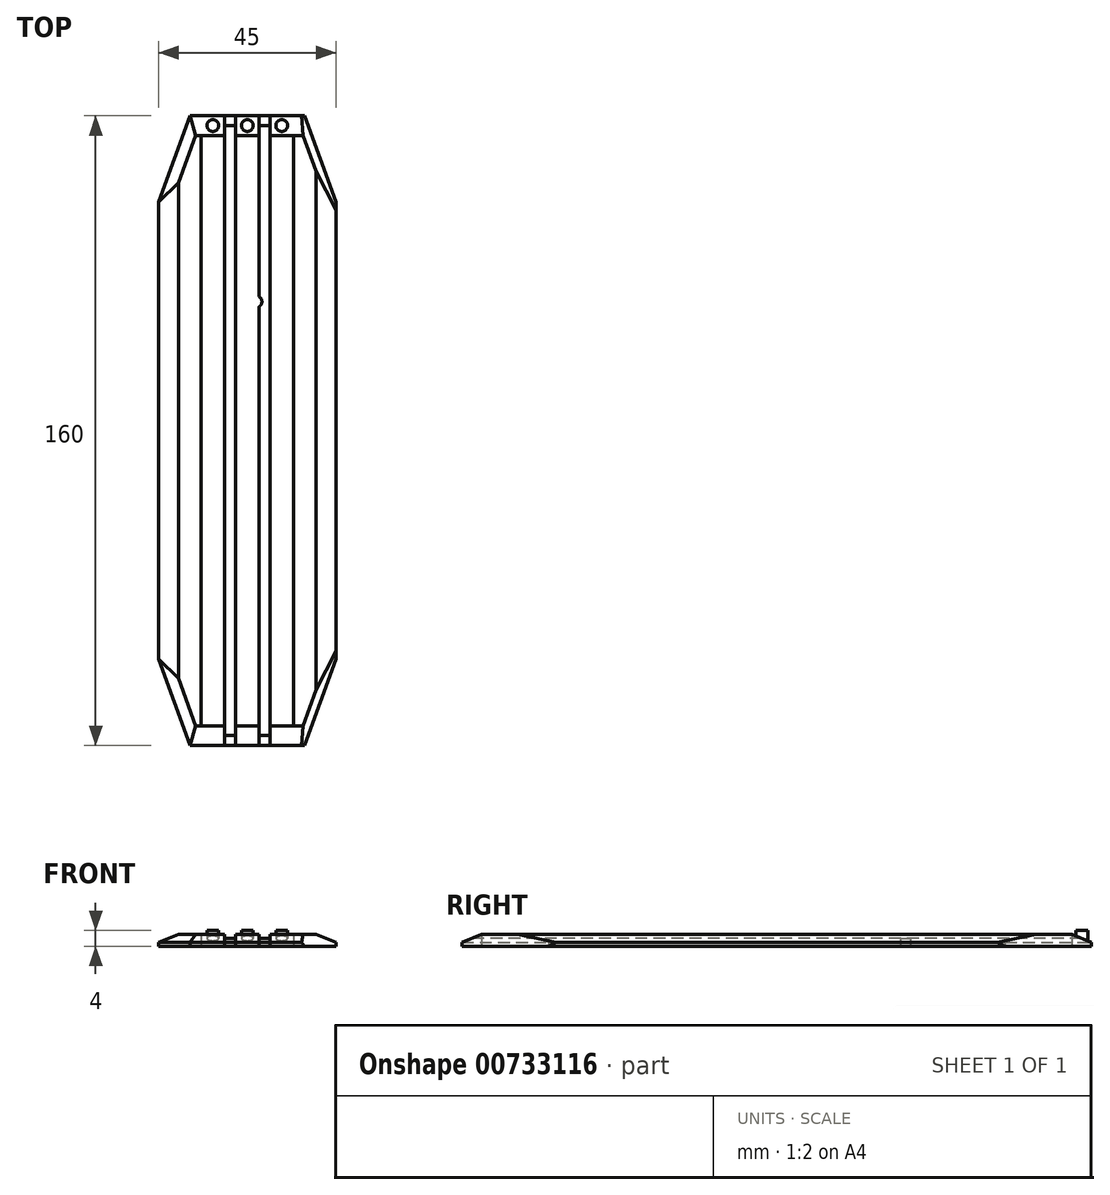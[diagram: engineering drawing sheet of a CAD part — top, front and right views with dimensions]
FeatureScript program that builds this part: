
annotation { "Feature Type Name" : "Feature", "Feature Type Description" : "" }
export const myFeature = defineFeature(function(context is Context, id is Id, definition is map)
    precondition{}
    {
        {
            var Q0;
            Q0=qCreatedBy(makeId("Top.planeOp"),FACE);
            var sketch = newSketch(context, id + "F0", { "sketchPlane" : qUnion([Q0])});
            skLineSegment(sketch, "E0.bottom", {"start": v(-22.12, 90) * mm, "end": v(22.88, 90) * mm});
            skLineSegment(sketch, "E0.top", {"start": v(-22.12, -70) * mm, "end": v(22.88, -70) * mm});
            skLineSegment(sketch, "E0.left", {"start": v(-22.12, 90) * mm, "end": v(-22.12, -70) * mm});
            skLineSegment(sketch, "E0.right", {"start": v(22.88, 90) * mm, "end": v(22.88, -70) * mm});
            skLineSegment(sketch, "E1", {"start": v(-22.12, 68) * mm, "end": v(-14.12, 90) * mm});
            skLineSegment(sketch, "E2", {"start": v(14.88, 90) * mm, "end": v(22.88, 68) * mm});
            skLineSegment(sketch, "E3", {"start": v(-22.12, -48) * mm, "end": v(-14.12, -70) * mm});
            skLineSegment(sketch, "E4", {"start": v(14.88, -70) * mm, "end": v(22.88, -48) * mm});
            skLineSegment(sketch, "E5", {"start": v(-11.37, 90) * mm, "end": v(-11.37, -70) * mm});
            skLineSegment(sketch, "E6", {"start": v(-5.37, 90) * mm, "end": v(-5.37, -70) * mm});
            skLineSegment(sketch, "E7", {"start": v(-2.62, 90) * mm, "end": v(-2.62, -70) * mm});
            skLineSegment(sketch, "E8", {"start": v(3.38, 90) * mm, "end": v(3.38, -70) * mm});
            skLineSegment(sketch, "E9", {"start": v(6.13, 90) * mm, "end": v(6.13, -70) * mm});
            skLineSegment(sketch, "E10", {"start": v(12.13, 90) * mm, "end": v(12.13, -70) * mm});
            skLineSegment(sketch, "E11", {"start": v(-22.12, 85) * mm, "end": v(22.88, 85) * mm});
            skLineSegment(sketch, "E12", {"start": v(-22.12, 80) * mm, "end": v(22.88, 80) * mm});
            skLineSegment(sketch, "E13", {"start": v(-22.12, 75) * mm, "end": v(22.88, 75) * mm});
            skLineSegment(sketch, "E14", {"start": v(-22.12, 70) * mm, "end": v(22.15, 70) * mm});
            skLineSegment(sketch, "E15", {"start": v(-22.12, 65) * mm, "end": v(22.88, 65) * mm});
            skLineSegment(sketch, "E16", {"start": v(-22.12, 60) * mm, "end": v(22.88, 60) * mm});
            skLineSegment(sketch, "E17", {"start": v(-22.12, 55) * mm, "end": v(22.88, 55) * mm});
            skLineSegment(sketch, "E18", {"start": v(-22.12, 50) * mm, "end": v(22.88, 50) * mm});
            skLineSegment(sketch, "E19", {"start": v(-22.12, 45) * mm, "end": v(22.88, 45) * mm});
            skLineSegment(sketch, "E20", {"start": v(-22.12, 40) * mm, "end": v(22.88, 40) * mm});
            skLineSegment(sketch, "E21", {"start": v(-22.12, 35) * mm, "end": v(22.88, 35) * mm});
            skLineSegment(sketch, "E22", {"start": v(-22.12, 30) * mm, "end": v(22.88, 30) * mm});
            skLineSegment(sketch, "E23", {"start": v(-22.12, 25) * mm, "end": v(22.88, 25) * mm});
            skLineSegment(sketch, "E24", {"start": v(-22.12, 20) * mm, "end": v(22.88, 20) * mm});
            skLineSegment(sketch, "E25", {"start": v(-22.12, 10) * mm, "end": v(22.88, 10) * mm});
            skLineSegment(sketch, "E26", {"start": v(-22.12, 5) * mm, "end": v(22.88, 5) * mm});
            skLineSegment(sketch, "E27", {"start": v(-22.12, 0) * mm, "end": v(22.88, 0) * mm});
            skLineSegment(sketch, "E28", {"start": v(-22.12, 15) * mm, "end": v(22.88, 15) * mm});
            skLineSegment(sketch, "E29", {"start": v(-22.12, -5) * mm, "end": v(22.88, -5) * mm});
            skLineSegment(sketch, "E30", {"start": v(-22.12, -10) * mm, "end": v(22.88, -10) * mm});
            skLineSegment(sketch, "E31", {"start": v(-22.12, -15) * mm, "end": v(22.88, -15) * mm});
            skLineSegment(sketch, "E32", {"start": v(-22.12, -20) * mm, "end": v(22.88, -20) * mm});
            skLineSegment(sketch, "E33", {"start": v(-22.12, -25) * mm, "end": v(22.88, -25) * mm});
            skLineSegment(sketch, "E34", {"start": v(-22.12, -30) * mm, "end": v(22.88, -30) * mm});
            skLineSegment(sketch, "E35", {"start": v(-22.12, -35) * mm, "end": v(22.88, -35) * mm});
            skLineSegment(sketch, "E36", {"start": v(-22.12, -40) * mm, "end": v(22.88, -40) * mm});
            skLineSegment(sketch, "E37", {"start": v(-22.12, -45) * mm, "end": v(22.88, -45) * mm});
            skLineSegment(sketch, "E38", {"start": v(-22.12, -50) * mm, "end": v(22.88, -50) * mm});
            skLineSegment(sketch, "E39", {"start": v(-22.12, -55) * mm, "end": v(22.88, -55) * mm});
            skLineSegment(sketch, "E40", {"start": v(-22.12, -60) * mm, "end": v(22.88, -60) * mm});
            skLineSegment(sketch, "E41", {"start": v(-22.12, -65) * mm, "end": v(22.88, -65) * mm});
            skCircle(sketch, "E42", {"center": v(-8.37, -62.5) * mm, "radius": 1.5 * mm});
            skLineSegment(sketch, "E43", {"start": v(-9.02, -61.15) * mm, "end": v(-7.02, -63.15) * mm});
            skLineSegment(sketch, "E44", {"start": v(-9.73, -61.85) * mm, "end": v(-7.73, -63.85) * mm});
            skLineSegment(sketch, "E45", {"start": v(-7.73, -61.15) * mm, "end": v(-9.73, -63.15) * mm});
            skLineSegment(sketch, "E46", {"start": v(-7.02, -61.85) * mm, "end": v(-9.02, -63.85) * mm});
            skCircle(sketch, "E47", {"center": v(9.13, -62.5) * mm, "radius": 1.5 * mm});
            skLineSegment(sketch, "E48", {"start": v(8.48, -61.15) * mm, "end": v(10.48, -63.15) * mm});
            skLineSegment(sketch, "E49", {"start": v(7.77, -61.85) * mm, "end": v(9.77, -63.85) * mm});
            skLineSegment(sketch, "E50", {"start": v(9.77, -61.15) * mm, "end": v(7.77, -63.15) * mm});
            skLineSegment(sketch, "E51", {"start": v(10.48, -61.85) * mm, "end": v(8.48, -63.85) * mm});
            skCircle(sketch, "E52", {"center": v(0.38, -62.5) * mm, "radius": 1.5 * mm});
            skLineSegment(sketch, "E53", {"start": v(-0.27, -61.15) * mm, "end": v(1.73, -63.15) * mm});
            skLineSegment(sketch, "E54", {"start": v(-0.98, -61.85) * mm, "end": v(1.02, -63.85) * mm});
            skLineSegment(sketch, "E55", {"start": v(1.02, -61.15) * mm, "end": v(-0.98, -63.15) * mm});
            skLineSegment(sketch, "E56", {"start": v(1.73, -61.85) * mm, "end": v(-0.27, -63.85) * mm});
            skCircle(sketch, "E57", {"center": v(9.19, -57.36) * mm, "radius": 1.5 * mm});
            skLineSegment(sketch, "E58", {"start": v(8.54, -56) * mm, "end": v(10.54, -58) * mm});
            skLineSegment(sketch, "E59", {"start": v(7.83, -56.7) * mm, "end": v(9.83, -58.7) * mm});
            skLineSegment(sketch, "E60", {"start": v(9.83, -56) * mm, "end": v(7.83, -58) * mm});
            skLineSegment(sketch, "E61", {"start": v(10.54, -56.7) * mm, "end": v(8.54, -58.7) * mm});
            skCircle(sketch, "E62", {"center": v(0.75, -56.96) * mm, "radius": 1.5 * mm});
            skLineSegment(sketch, "E63", {"start": v(0.1, -55.6) * mm, "end": v(2.1, -57.6) * mm});
            skLineSegment(sketch, "E64", {"start": v(-0.6, -56.31) * mm, "end": v(1.4, -58.31) * mm});
            skLineSegment(sketch, "E65", {"start": v(1.4, -55.6) * mm, "end": v(-0.6, -57.6) * mm});
            skLineSegment(sketch, "E66", {"start": v(2.1, -56.31) * mm, "end": v(0.1, -58.31) * mm});
            skCircle(sketch, "E67", {"center": v(-8.3, -57.32) * mm, "radius": 1.5 * mm});
            skLineSegment(sketch, "E68", {"start": v(-8.95, -55.97) * mm, "end": v(-6.95, -57.97) * mm});
            skLineSegment(sketch, "E69", {"start": v(-9.66, -56.68) * mm, "end": v(-7.66, -58.68) * mm});
            skLineSegment(sketch, "E70", {"start": v(-7.66, -55.97) * mm, "end": v(-9.66, -57.97) * mm});
            skLineSegment(sketch, "E71", {"start": v(-6.95, -56.68) * mm, "end": v(-8.95, -58.68) * mm});
            skCircle(sketch, "E72", {"center": v(-8.54, -52.38) * mm, "radius": 1.5 * mm});
            skLineSegment(sketch, "E73", {"start": v(-9.19, -51.03) * mm, "end": v(-7.19, -53.03) * mm});
            skLineSegment(sketch, "E74", {"start": v(-9.9, -51.74) * mm, "end": v(-7.9, -53.74) * mm});
            skLineSegment(sketch, "E75", {"start": v(-7.9, -51.03) * mm, "end": v(-9.9, -53.03) * mm});
            skLineSegment(sketch, "E76", {"start": v(-7.19, -51.74) * mm, "end": v(-9.19, -53.74) * mm});
            skCircle(sketch, "E77", {"center": v(0.5, -52.63) * mm, "radius": 1.5 * mm});
            skLineSegment(sketch, "E78", {"start": v(-0.15, -51.28) * mm, "end": v(1.85, -53.28) * mm});
            skLineSegment(sketch, "E79", {"start": v(-0.85, -51.99) * mm, "end": v(1.15, -53.99) * mm});
            skLineSegment(sketch, "E80", {"start": v(1.15, -51.28) * mm, "end": v(-0.85, -53.28) * mm});
            skLineSegment(sketch, "E81", {"start": v(1.85, -51.99) * mm, "end": v(-0.15, -53.99) * mm});
            skCircle(sketch, "E82", {"center": v(9.29, -52.38) * mm, "radius": 1.5 * mm});
            skLineSegment(sketch, "E83", {"start": v(8.64, -51.03) * mm, "end": v(10.64, -53.03) * mm});
            skLineSegment(sketch, "E84", {"start": v(7.94, -51.74) * mm, "end": v(9.94, -53.74) * mm});
            skLineSegment(sketch, "E85", {"start": v(9.94, -51.03) * mm, "end": v(7.94, -53.03) * mm});
            skLineSegment(sketch, "E86", {"start": v(10.64, -51.74) * mm, "end": v(8.64, -53.74) * mm});
            skCircle(sketch, "E87", {"center": v(9.04, -47.23) * mm, "radius": 1.5 * mm});
            skLineSegment(sketch, "E88", {"start": v(8.4, -45.88) * mm, "end": v(10.4, -47.88) * mm});
            skLineSegment(sketch, "E89", {"start": v(7.68, -46.59) * mm, "end": v(9.68, -48.59) * mm});
            skLineSegment(sketch, "E90", {"start": v(9.68, -45.88) * mm, "end": v(7.68, -47.88) * mm});
            skLineSegment(sketch, "E91", {"start": v(10.4, -46.59) * mm, "end": v(8.4, -48.59) * mm});
            skCircle(sketch, "E92", {"center": v(0.04, -47.48) * mm, "radius": 1.5 * mm});
            skLineSegment(sketch, "E93", {"start": v(-0.6, -46.13) * mm, "end": v(1.4, -48.13) * mm});
            skLineSegment(sketch, "E94", {"start": v(-1.32, -46.84) * mm, "end": v(0.68, -48.84) * mm});
            skLineSegment(sketch, "E95", {"start": v(0.68, -46.13) * mm, "end": v(-1.32, -48.13) * mm});
            skLineSegment(sketch, "E96", {"start": v(1.4, -46.84) * mm, "end": v(-0.6, -48.84) * mm});
            skCircle(sketch, "E97", {"center": v(-7.79, -47.1) * mm, "radius": 1.5 * mm});
            skLineSegment(sketch, "E98", {"start": v(-8.43, -45.75) * mm, "end": v(-6.43, -47.75) * mm});
            skLineSegment(sketch, "E99", {"start": v(-9.14, -46.46) * mm, "end": v(-7.14, -48.46) * mm});
            skLineSegment(sketch, "E100", {"start": v(-7.14, -45.75) * mm, "end": v(-9.14, -47.75) * mm});
            skLineSegment(sketch, "E101", {"start": v(-6.43, -46.46) * mm, "end": v(-8.43, -48.46) * mm});
            skCircle(sketch, "E102", {"center": v(-8.3, -42.65) * mm, "radius": 1.5 * mm});
            skLineSegment(sketch, "E103", {"start": v(-8.94, -41.3) * mm, "end": v(-6.94, -43.3) * mm});
            skLineSegment(sketch, "E104", {"start": v(-9.64, -42) * mm, "end": v(-7.64, -44) * mm});
            skLineSegment(sketch, "E105", {"start": v(-7.64, -41.3) * mm, "end": v(-9.64, -43.3) * mm});
            skLineSegment(sketch, "E106", {"start": v(-6.94, -42) * mm, "end": v(-8.94, -44) * mm});
            skCircle(sketch, "E107", {"center": v(-8.67, -37.44) * mm, "radius": 1.5 * mm});
            skLineSegment(sketch, "E108", {"start": v(-9.31, -36.09) * mm, "end": v(-7.31, -38.09) * mm});
            skLineSegment(sketch, "E109", {"start": v(-10.02, -36.8) * mm, "end": v(-8.02, -38.8) * mm});
            skLineSegment(sketch, "E110", {"start": v(-8.02, -36.09) * mm, "end": v(-10.02, -38.09) * mm});
            skLineSegment(sketch, "E111", {"start": v(-7.31, -36.8) * mm, "end": v(-9.31, -38.8) * mm});
            skCircle(sketch, "E112", {"center": v(-8.3, -32.42) * mm, "radius": 1.5 * mm});
            skLineSegment(sketch, "E113", {"start": v(-8.94, -31.06) * mm, "end": v(-6.94, -33.06) * mm});
            skLineSegment(sketch, "E114", {"start": v(-9.64, -31.77) * mm, "end": v(-7.64, -33.77) * mm});
            skLineSegment(sketch, "E115", {"start": v(-7.64, -31.06) * mm, "end": v(-9.64, -33.06) * mm});
            skLineSegment(sketch, "E116", {"start": v(-6.94, -31.77) * mm, "end": v(-8.94, -33.77) * mm});
            skCircle(sketch, "E117", {"center": v(-8.42, -27.14) * mm, "radius": 1.5 * mm});
            skLineSegment(sketch, "E118", {"start": v(-9.06, -25.79) * mm, "end": v(-7.06, -27.79) * mm});
            skLineSegment(sketch, "E119", {"start": v(-9.77, -26.5) * mm, "end": v(-7.77, -28.5) * mm});
            skLineSegment(sketch, "E120", {"start": v(-7.77, -25.79) * mm, "end": v(-9.77, -27.79) * mm});
            skLineSegment(sketch, "E121", {"start": v(-7.06, -26.5) * mm, "end": v(-9.06, -28.5) * mm});
            skCircle(sketch, "E122", {"center": v(0.06, -27.52) * mm, "radius": 1.5 * mm});
            skLineSegment(sketch, "E123", {"start": v(-0.59, -26.16) * mm, "end": v(1.41, -28.16) * mm});
            skLineSegment(sketch, "E124", {"start": v(-1.3, -26.87) * mm, "end": v(0.7, -28.87) * mm});
            skLineSegment(sketch, "E125", {"start": v(0.7, -26.16) * mm, "end": v(-1.3, -28.16) * mm});
            skLineSegment(sketch, "E126", {"start": v(1.41, -26.87) * mm, "end": v(-0.59, -28.87) * mm});
            skCircle(sketch, "E127", {"center": v(0.06, -32.35) * mm, "radius": 1.5 * mm});
            skLineSegment(sketch, "E128", {"start": v(-0.59, -31) * mm, "end": v(1.41, -33) * mm});
            skLineSegment(sketch, "E129", {"start": v(-1.3, -31.7) * mm, "end": v(0.7, -33.7) * mm});
            skLineSegment(sketch, "E130", {"start": v(0.7, -31) * mm, "end": v(-1.3, -33) * mm});
            skLineSegment(sketch, "E131", {"start": v(1.41, -31.7) * mm, "end": v(-0.59, -33.7) * mm});
            skCircle(sketch, "E132", {"center": v(0.25, -37.44) * mm, "radius": 1.5 * mm});
            skLineSegment(sketch, "E133", {"start": v(-0.4, -36.09) * mm, "end": v(1.6, -38.09) * mm});
            skLineSegment(sketch, "E134", {"start": v(-1.1, -36.8) * mm, "end": v(0.9, -38.8) * mm});
            skLineSegment(sketch, "E135", {"start": v(0.9, -36.09) * mm, "end": v(-1.1, -38.09) * mm});
            skLineSegment(sketch, "E136", {"start": v(1.6, -36.8) * mm, "end": v(-0.4, -38.8) * mm});
            skCircle(sketch, "E137", {"center": v(0.37, -42.4) * mm, "radius": 1.5 * mm});
            skLineSegment(sketch, "E138", {"start": v(-0.27, -41.05) * mm, "end": v(1.73, -43.05) * mm});
            skLineSegment(sketch, "E139", {"start": v(-0.98, -41.75) * mm, "end": v(1.02, -43.75) * mm});
            skLineSegment(sketch, "E140", {"start": v(1.02, -41.05) * mm, "end": v(-0.98, -43.05) * mm});
            skLineSegment(sketch, "E141", {"start": v(1.73, -41.75) * mm, "end": v(-0.27, -43.75) * mm});
            skCircle(sketch, "E142", {"center": v(9.8, -42.08) * mm, "radius": 1.5 * mm});
            skLineSegment(sketch, "E143", {"start": v(9.15, -40.73) * mm, "end": v(11.15, -42.73) * mm});
            skLineSegment(sketch, "E144", {"start": v(8.44, -41.44) * mm, "end": v(10.44, -43.44) * mm});
            skLineSegment(sketch, "E145", {"start": v(10.44, -40.73) * mm, "end": v(8.44, -42.73) * mm});
            skLineSegment(sketch, "E146", {"start": v(11.15, -41.44) * mm, "end": v(9.15, -43.44) * mm});
            skCircle(sketch, "E147", {"center": v(9.29, -37.06) * mm, "radius": 1.5 * mm});
            skLineSegment(sketch, "E148", {"start": v(8.64, -35.7) * mm, "end": v(10.64, -37.7) * mm});
            skLineSegment(sketch, "E149", {"start": v(7.94, -36.42) * mm, "end": v(9.94, -38.42) * mm});
            skLineSegment(sketch, "E150", {"start": v(9.94, -35.7) * mm, "end": v(7.94, -37.7) * mm});
            skLineSegment(sketch, "E151", {"start": v(10.64, -36.42) * mm, "end": v(8.64, -38.42) * mm});
            skCircle(sketch, "E152", {"center": v(9.35, -32.1) * mm, "radius": 1.5 * mm});
            skLineSegment(sketch, "E153", {"start": v(8.7, -30.75) * mm, "end": v(10.7, -32.75) * mm});
            skLineSegment(sketch, "E154", {"start": v(8, -31.46) * mm, "end": v(10, -33.46) * mm});
            skLineSegment(sketch, "E155", {"start": v(10, -30.75) * mm, "end": v(8, -32.75) * mm});
            skLineSegment(sketch, "E156", {"start": v(10.7, -31.46) * mm, "end": v(8.7, -33.46) * mm});
            skCircle(sketch, "E157", {"center": v(9.04, -27.77) * mm, "radius": 1.5 * mm});
            skLineSegment(sketch, "E158", {"start": v(8.4, -26.42) * mm, "end": v(10.4, -28.42) * mm});
            skLineSegment(sketch, "E159", {"start": v(7.68, -27.12) * mm, "end": v(9.68, -29.12) * mm});
            skLineSegment(sketch, "E160", {"start": v(9.68, -26.42) * mm, "end": v(7.68, -28.42) * mm});
            skLineSegment(sketch, "E161", {"start": v(10.4, -27.12) * mm, "end": v(8.4, -29.12) * mm});
            skCircle(sketch, "E162", {"center": v(9.1, -22.4) * mm, "radius": 1.5 * mm});
            skLineSegment(sketch, "E163", {"start": v(8.45, -21.05) * mm, "end": v(10.45, -23.05) * mm});
            skLineSegment(sketch, "E164", {"start": v(7.74, -21.75) * mm, "end": v(9.74, -23.75) * mm});
            skLineSegment(sketch, "E165", {"start": v(9.74, -21.05) * mm, "end": v(7.74, -23.05) * mm});
            skLineSegment(sketch, "E166", {"start": v(10.45, -21.75) * mm, "end": v(8.45, -23.75) * mm});
            skCircle(sketch, "E167", {"center": v(9.15, -17.23) * mm, "radius": 1.5 * mm});
            skLineSegment(sketch, "E168", {"start": v(8.5, -15.87) * mm, "end": v(10.5, -17.87) * mm});
            skLineSegment(sketch, "E169", {"start": v(7.8, -16.58) * mm, "end": v(9.8, -18.58) * mm});
            skLineSegment(sketch, "E170", {"start": v(9.8, -15.87) * mm, "end": v(7.8, -17.87) * mm});
            skLineSegment(sketch, "E171", {"start": v(10.5, -16.58) * mm, "end": v(8.5, -18.58) * mm});
            skCircle(sketch, "E172", {"center": v(8.91, -12.1) * mm, "radius": 1.5 * mm});
            skLineSegment(sketch, "E173", {"start": v(8.26, -10.75) * mm, "end": v(10.26, -12.75) * mm});
            skLineSegment(sketch, "E174", {"start": v(7.56, -11.46) * mm, "end": v(9.56, -13.46) * mm});
            skLineSegment(sketch, "E175", {"start": v(9.56, -10.75) * mm, "end": v(7.56, -12.75) * mm});
            skLineSegment(sketch, "E176", {"start": v(10.26, -11.46) * mm, "end": v(8.26, -13.46) * mm});
            skCircle(sketch, "E177", {"center": v(8.91, -6.98) * mm, "radius": 1.5 * mm});
            skLineSegment(sketch, "E178", {"start": v(8.26, -5.63) * mm, "end": v(10.26, -7.63) * mm});
            skLineSegment(sketch, "E179", {"start": v(7.56, -6.33) * mm, "end": v(9.56, -8.33) * mm});
            skLineSegment(sketch, "E180", {"start": v(9.56, -5.63) * mm, "end": v(7.56, -7.63) * mm});
            skLineSegment(sketch, "E181", {"start": v(10.26, -6.33) * mm, "end": v(8.26, -8.33) * mm});
            skCircle(sketch, "E182", {"center": v(8.67, -2.47) * mm, "radius": 1.5 * mm});
            skLineSegment(sketch, "E183", {"start": v(8.02, -1.11) * mm, "end": v(10.02, -3.11) * mm});
            skLineSegment(sketch, "E184", {"start": v(7.31, -1.82) * mm, "end": v(9.31, -3.82) * mm});
            skLineSegment(sketch, "E185", {"start": v(9.31, -1.11) * mm, "end": v(7.31, -3.11) * mm});
            skLineSegment(sketch, "E186", {"start": v(10.02, -1.82) * mm, "end": v(8.02, -3.82) * mm});
            skCircle(sketch, "E187", {"center": v(8.54, 2.05) * mm, "radius": 1.5 * mm});
            skLineSegment(sketch, "E188", {"start": v(7.9, 3.4) * mm, "end": v(9.9, 1.4) * mm});
            skLineSegment(sketch, "E189", {"start": v(7.2, 2.7) * mm, "end": v(9.2, 0.7) * mm});
            skLineSegment(sketch, "E190", {"start": v(9.2, 3.4) * mm, "end": v(7.2, 1.4) * mm});
            skLineSegment(sketch, "E191", {"start": v(9.9, 2.7) * mm, "end": v(7.9, 0.7) * mm});
            skCircle(sketch, "E192", {"center": v(-0.3, 2.54) * mm, "radius": 1.5 * mm});
            skLineSegment(sketch, "E193", {"start": v(-0.95, 3.9) * mm, "end": v(1.05, 1.9) * mm});
            skLineSegment(sketch, "E194", {"start": v(-1.65, 3.18) * mm, "end": v(0.35, 1.18) * mm});
            skLineSegment(sketch, "E195", {"start": v(0.35, 3.9) * mm, "end": v(-1.65, 1.9) * mm});
            skLineSegment(sketch, "E196", {"start": v(1.05, 3.18) * mm, "end": v(-0.95, 1.18) * mm});
            skCircle(sketch, "E197", {"center": v(0.19, -3.5) * mm, "radius": 1.5 * mm});
            skLineSegment(sketch, "E198", {"start": v(-0.46, -2.15) * mm, "end": v(1.54, -4.15) * mm});
            skLineSegment(sketch, "E199", {"start": v(-1.17, -2.86) * mm, "end": v(0.83, -4.86) * mm});
            skLineSegment(sketch, "E200", {"start": v(0.83, -2.15) * mm, "end": v(-1.17, -4.15) * mm});
            skLineSegment(sketch, "E201", {"start": v(1.54, -2.86) * mm, "end": v(-0.46, -4.86) * mm});
            skCircle(sketch, "E202", {"center": v(0.13, -7.22) * mm, "radius": 1.5 * mm});
            skLineSegment(sketch, "E203", {"start": v(-0.52, -5.87) * mm, "end": v(1.48, -7.87) * mm});
            skLineSegment(sketch, "E204", {"start": v(-1.23, -6.58) * mm, "end": v(0.77, -8.58) * mm});
            skLineSegment(sketch, "E205", {"start": v(0.77, -5.87) * mm, "end": v(-1.23, -7.87) * mm});
            skLineSegment(sketch, "E206", {"start": v(1.48, -6.58) * mm, "end": v(-0.52, -8.58) * mm});
            skCircle(sketch, "E207", {"center": v(0.86, -13.44) * mm, "radius": 1.5 * mm});
            skLineSegment(sketch, "E208", {"start": v(0.21, -12.1) * mm, "end": v(2.21, -14.1) * mm});
            skLineSegment(sketch, "E209", {"start": v(-0.5, -12.8) * mm, "end": v(1.5, -14.8) * mm});
            skLineSegment(sketch, "E210", {"start": v(1.5, -12.1) * mm, "end": v(-0.5, -14.1) * mm});
            skLineSegment(sketch, "E211", {"start": v(2.21, -12.8) * mm, "end": v(0.21, -14.8) * mm});
            skCircle(sketch, "E212", {"center": v(0.5, -17.35) * mm, "radius": 1.5 * mm});
            skLineSegment(sketch, "E213", {"start": v(-0.15, -16) * mm, "end": v(1.85, -18) * mm});
            skLineSegment(sketch, "E214", {"start": v(-0.86, -16.7) * mm, "end": v(1.14, -18.7) * mm});
            skLineSegment(sketch, "E215", {"start": v(1.14, -16) * mm, "end": v(-0.86, -18) * mm});
            skLineSegment(sketch, "E216", {"start": v(1.85, -16.7) * mm, "end": v(-0.15, -18.7) * mm});
            skCircle(sketch, "E217", {"center": v(0.37, -22.05) * mm, "radius": 1.5 * mm});
            skLineSegment(sketch, "E218", {"start": v(-0.28, -20.7) * mm, "end": v(1.72, -22.7) * mm});
            skLineSegment(sketch, "E219", {"start": v(-0.98, -21.4) * mm, "end": v(1.02, -23.4) * mm});
            skLineSegment(sketch, "E220", {"start": v(1.02, -20.7) * mm, "end": v(-0.98, -22.7) * mm});
            skLineSegment(sketch, "E221", {"start": v(1.72, -21.4) * mm, "end": v(-0.28, -23.4) * mm});
            skCircle(sketch, "E222", {"center": v(-8.78, -22.47) * mm, "radius": 1.5 * mm});
            skLineSegment(sketch, "E223", {"start": v(-9.43, -21.12) * mm, "end": v(-7.43, -23.12) * mm});
            skLineSegment(sketch, "E224", {"start": v(-10.13, -21.83) * mm, "end": v(-8.13, -23.83) * mm});
            skLineSegment(sketch, "E225", {"start": v(-8.13, -21.12) * mm, "end": v(-10.13, -23.12) * mm});
            skLineSegment(sketch, "E226", {"start": v(-7.43, -21.83) * mm, "end": v(-9.43, -23.83) * mm});
            skCircle(sketch, "E227", {"center": v(-8.35, -17.9) * mm, "radius": 1.5 * mm});
            skLineSegment(sketch, "E228", {"start": v(-9, -16.54) * mm, "end": v(-7, -18.54) * mm});
            skLineSegment(sketch, "E229", {"start": v(-9.7, -17.25) * mm, "end": v(-7.7, -19.25) * mm});
            skLineSegment(sketch, "E230", {"start": v(-7.7, -16.54) * mm, "end": v(-9.7, -18.54) * mm});
            skLineSegment(sketch, "E231", {"start": v(-7, -17.25) * mm, "end": v(-9, -19.25) * mm});
            skCircle(sketch, "E232", {"center": v(-8.41, -12.6) * mm, "radius": 1.5 * mm});
            skLineSegment(sketch, "E233", {"start": v(-9.06, -11.24) * mm, "end": v(-7.06, -13.24) * mm});
            skLineSegment(sketch, "E234", {"start": v(-9.77, -11.94) * mm, "end": v(-7.77, -13.94) * mm});
            skLineSegment(sketch, "E235", {"start": v(-7.77, -11.24) * mm, "end": v(-9.77, -13.24) * mm});
            skLineSegment(sketch, "E236", {"start": v(-7.06, -11.94) * mm, "end": v(-9.06, -13.94) * mm});
            skCircle(sketch, "E237", {"center": v(-8.17, -6.74) * mm, "radius": 1.5 * mm});
            skLineSegment(sketch, "E238", {"start": v(-8.82, -5.38) * mm, "end": v(-6.82, -7.38) * mm});
            skLineSegment(sketch, "E239", {"start": v(-9.52, -6.09) * mm, "end": v(-7.52, -8.09) * mm});
            skLineSegment(sketch, "E240", {"start": v(-7.52, -5.38) * mm, "end": v(-9.52, -7.38) * mm});
            skLineSegment(sketch, "E241", {"start": v(-6.82, -6.09) * mm, "end": v(-8.82, -8.09) * mm});
            skCircle(sketch, "E242", {"center": v(-7.92, -2.83) * mm, "radius": 1.5 * mm});
            skLineSegment(sketch, "E243", {"start": v(-8.57, -1.48) * mm, "end": v(-6.57, -3.48) * mm});
            skLineSegment(sketch, "E244", {"start": v(-9.28, -2.18) * mm, "end": v(-7.28, -4.18) * mm});
            skLineSegment(sketch, "E245", {"start": v(-7.28, -1.48) * mm, "end": v(-9.28, -3.48) * mm});
            skLineSegment(sketch, "E246", {"start": v(-6.57, -2.18) * mm, "end": v(-8.57, -4.18) * mm});
            skCircle(sketch, "E247", {"center": v(-8.17, 2.6) * mm, "radius": 1.5 * mm});
            skLineSegment(sketch, "E248", {"start": v(-8.82, 3.95) * mm, "end": v(-6.82, 1.95) * mm});
            skLineSegment(sketch, "E249", {"start": v(-9.52, 3.24) * mm, "end": v(-7.52, 1.24) * mm});
            skLineSegment(sketch, "E250", {"start": v(-7.52, 3.95) * mm, "end": v(-9.52, 1.95) * mm});
            skLineSegment(sketch, "E251", {"start": v(-6.82, 3.24) * mm, "end": v(-8.82, 1.24) * mm});
            skCircle(sketch, "E252", {"center": v(-7.86, 7.54) * mm, "radius": 1.5 * mm});
            skLineSegment(sketch, "E253", {"start": v(-8.51, 8.9) * mm, "end": v(-6.51, 6.9) * mm});
            skLineSegment(sketch, "E254", {"start": v(-9.22, 8.18) * mm, "end": v(-7.22, 6.18) * mm});
            skLineSegment(sketch, "E255", {"start": v(-7.22, 8.9) * mm, "end": v(-9.22, 6.9) * mm});
            skLineSegment(sketch, "E256", {"start": v(-6.51, 8.18) * mm, "end": v(-8.51, 6.18) * mm});
            skCircle(sketch, "E257", {"center": v(0.37, 8.2) * mm, "radius": 1.5 * mm});
            skLineSegment(sketch, "E258", {"start": v(-0.28, 9.56) * mm, "end": v(1.72, 7.56) * mm});
            skLineSegment(sketch, "E259", {"start": v(-0.98, 8.86) * mm, "end": v(1.02, 6.86) * mm});
            skLineSegment(sketch, "E260", {"start": v(1.02, 9.56) * mm, "end": v(-0.98, 7.56) * mm});
            skLineSegment(sketch, "E261", {"start": v(1.72, 8.86) * mm, "end": v(-0.28, 6.86) * mm});
            skCircle(sketch, "E262", {"center": v(9.7, 7.42) * mm, "radius": 1.5 * mm});
            skLineSegment(sketch, "E263", {"start": v(9.06, 8.77) * mm, "end": v(11.06, 6.77) * mm});
            skLineSegment(sketch, "E264", {"start": v(8.35, 8.06) * mm, "end": v(10.35, 6.06) * mm});
            skLineSegment(sketch, "E265", {"start": v(10.35, 8.77) * mm, "end": v(8.35, 6.77) * mm});
            skLineSegment(sketch, "E266", {"start": v(11.06, 8.06) * mm, "end": v(9.06, 6.06) * mm});
            skCircle(sketch, "E267", {"center": v(8.93, 12.21) * mm, "radius": 1.5 * mm});
            skLineSegment(sketch, "E268", {"start": v(8.29, 13.57) * mm, "end": v(10.29, 11.57) * mm});
            skLineSegment(sketch, "E269", {"start": v(7.58, 12.86) * mm, "end": v(9.58, 10.86) * mm});
            skLineSegment(sketch, "E270", {"start": v(9.58, 13.57) * mm, "end": v(7.58, 11.57) * mm});
            skLineSegment(sketch, "E271", {"start": v(10.29, 12.86) * mm, "end": v(8.29, 10.86) * mm});
            skCircle(sketch, "E272", {"center": v(0.05, 11.91) * mm, "radius": 1.5 * mm});
            skLineSegment(sketch, "E273", {"start": v(-0.6, 13.27) * mm, "end": v(1.4, 11.27) * mm});
            skLineSegment(sketch, "E274", {"start": v(-1.3, 12.56) * mm, "end": v(0.7, 10.56) * mm});
            skLineSegment(sketch, "E275", {"start": v(0.7, 13.27) * mm, "end": v(-1.3, 11.27) * mm});
            skLineSegment(sketch, "E276", {"start": v(1.4, 12.56) * mm, "end": v(-0.6, 10.56) * mm});
            skCircle(sketch, "E277", {"center": v(-8.76, 12.96) * mm, "radius": 1.5 * mm});
            skLineSegment(sketch, "E278", {"start": v(-9.4, 14.31) * mm, "end": v(-7.4, 12.31) * mm});
            skLineSegment(sketch, "E279", {"start": v(-10.12, 13.6) * mm, "end": v(-8.12, 11.6) * mm});
            skLineSegment(sketch, "E280", {"start": v(-8.12, 14.31) * mm, "end": v(-10.12, 12.31) * mm});
            skLineSegment(sketch, "E281", {"start": v(-7.4, 13.6) * mm, "end": v(-9.4, 11.6) * mm});
            skCircle(sketch, "E282", {"center": v(-8.1, 17.51) * mm, "radius": 1.5 * mm});
            skLineSegment(sketch, "E283", {"start": v(-8.74, 18.87) * mm, "end": v(-6.74, 16.87) * mm});
            skLineSegment(sketch, "E284", {"start": v(-9.44, 18.16) * mm, "end": v(-7.44, 16.16) * mm});
            skLineSegment(sketch, "E285", {"start": v(-7.44, 18.87) * mm, "end": v(-9.44, 16.87) * mm});
            skLineSegment(sketch, "E286", {"start": v(-6.74, 18.16) * mm, "end": v(-8.74, 16.16) * mm});
            skCircle(sketch, "E287", {"center": v(0.2, 17.44) * mm, "radius": 1.5 * mm});
            skLineSegment(sketch, "E288", {"start": v(-0.45, 18.8) * mm, "end": v(1.55, 16.8) * mm});
            skLineSegment(sketch, "E289", {"start": v(-1.16, 18.09) * mm, "end": v(0.84, 16.09) * mm});
            skLineSegment(sketch, "E290", {"start": v(0.84, 18.8) * mm, "end": v(-1.16, 16.8) * mm});
            skLineSegment(sketch, "E291", {"start": v(1.55, 18.09) * mm, "end": v(-0.45, 16.09) * mm});
            skCircle(sketch, "E292", {"center": v(8.86, 17.59) * mm, "radius": 1.5 * mm});
            skLineSegment(sketch, "E293", {"start": v(8.21, 18.94) * mm, "end": v(10.21, 16.94) * mm});
            skLineSegment(sketch, "E294", {"start": v(7.5, 18.23) * mm, "end": v(9.5, 16.23) * mm});
            skLineSegment(sketch, "E295", {"start": v(9.5, 18.94) * mm, "end": v(7.5, 16.94) * mm});
            skLineSegment(sketch, "E296", {"start": v(10.21, 18.23) * mm, "end": v(8.21, 16.23) * mm});
            skCircle(sketch, "E297", {"center": v(9, 22.52) * mm, "radius": 1.5 * mm});
            skLineSegment(sketch, "E298", {"start": v(8.36, 23.87) * mm, "end": v(10.36, 21.87) * mm});
            skLineSegment(sketch, "E299", {"start": v(7.65, 23.16) * mm, "end": v(9.65, 21.16) * mm});
            skLineSegment(sketch, "E300", {"start": v(9.65, 23.87) * mm, "end": v(7.65, 21.87) * mm});
            skLineSegment(sketch, "E301", {"start": v(10.36, 23.16) * mm, "end": v(8.36, 21.16) * mm});
            skCircle(sketch, "E302", {"center": v(0.05, 22.3) * mm, "radius": 1.5 * mm});
            skLineSegment(sketch, "E303", {"start": v(-0.6, 23.65) * mm, "end": v(1.4, 21.65) * mm});
            skLineSegment(sketch, "E304", {"start": v(-1.3, 22.94) * mm, "end": v(0.7, 20.94) * mm});
            skLineSegment(sketch, "E305", {"start": v(0.7, 23.65) * mm, "end": v(-1.3, 21.65) * mm});
            skLineSegment(sketch, "E306", {"start": v(1.4, 22.94) * mm, "end": v(-0.6, 20.94) * mm});
            skCircle(sketch, "E307", {"center": v(-8.61, 22.37) * mm, "radius": 1.5 * mm});
            skLineSegment(sketch, "E308", {"start": v(-9.26, 23.72) * mm, "end": v(-7.26, 21.72) * mm});
            skLineSegment(sketch, "E309", {"start": v(-9.97, 23.01) * mm, "end": v(-7.97, 21.01) * mm});
            skLineSegment(sketch, "E310", {"start": v(-7.97, 23.72) * mm, "end": v(-9.97, 21.72) * mm});
            skLineSegment(sketch, "E311", {"start": v(-7.26, 23.01) * mm, "end": v(-9.26, 21.01) * mm});
            skCircle(sketch, "E312", {"center": v(-8.46, 27.9) * mm, "radius": 1.5 * mm});
            skLineSegment(sketch, "E313", {"start": v(-9.11, 29.25) * mm, "end": v(-7.11, 27.25) * mm});
            skLineSegment(sketch, "E314", {"start": v(-9.82, 28.54) * mm, "end": v(-7.82, 26.54) * mm});
            skLineSegment(sketch, "E315", {"start": v(-7.82, 29.25) * mm, "end": v(-9.82, 27.25) * mm});
            skLineSegment(sketch, "E316", {"start": v(-7.11, 28.54) * mm, "end": v(-9.11, 26.54) * mm});
            skCircle(sketch, "E317", {"center": v(0.64, 27.74) * mm, "radius": 1.5 * mm});
            skLineSegment(sketch, "E318", {"start": v(0, 29.1) * mm, "end": v(2, 27.1) * mm});
            skLineSegment(sketch, "E319", {"start": v(-0.7, 28.39) * mm, "end": v(1.3, 26.39) * mm});
            skLineSegment(sketch, "E320", {"start": v(1.3, 29.1) * mm, "end": v(-0.7, 27.1) * mm});
            skLineSegment(sketch, "E321", {"start": v(2, 28.39) * mm, "end": v(0, 26.39) * mm});
            skCircle(sketch, "E322", {"center": v(9.46, 27.6) * mm, "radius": 1.5 * mm});
            skLineSegment(sketch, "E323", {"start": v(8.8, 28.95) * mm, "end": v(10.8, 26.95) * mm});
            skLineSegment(sketch, "E324", {"start": v(8.1, 28.24) * mm, "end": v(10.1, 26.24) * mm});
            skLineSegment(sketch, "E325", {"start": v(10.1, 28.95) * mm, "end": v(8.1, 26.95) * mm});
            skLineSegment(sketch, "E326", {"start": v(10.8, 28.24) * mm, "end": v(8.8, 26.24) * mm});
            skCircle(sketch, "E327", {"center": v(9.16, 32.97) * mm, "radius": 1.5 * mm});
            skLineSegment(sketch, "E328", {"start": v(8.51, 34.32) * mm, "end": v(10.51, 32.32) * mm});
            skLineSegment(sketch, "E329", {"start": v(7.8, 33.62) * mm, "end": v(9.8, 31.62) * mm});
            skLineSegment(sketch, "E330", {"start": v(9.8, 34.32) * mm, "end": v(7.8, 32.32) * mm});
            skLineSegment(sketch, "E331", {"start": v(10.51, 33.62) * mm, "end": v(8.51, 31.62) * mm});
            skCircle(sketch, "E332", {"center": v(0.27, 32.97) * mm, "radius": 1.5 * mm});
            skLineSegment(sketch, "E333", {"start": v(-0.38, 34.32) * mm, "end": v(1.62, 32.32) * mm});
            skLineSegment(sketch, "E334", {"start": v(-1.08, 33.62) * mm, "end": v(0.92, 31.62) * mm});
            skLineSegment(sketch, "E335", {"start": v(0.92, 34.32) * mm, "end": v(-1.08, 32.32) * mm});
            skLineSegment(sketch, "E336", {"start": v(1.62, 33.62) * mm, "end": v(-0.38, 31.62) * mm});
            skCircle(sketch, "E337", {"center": v(-8.46, 32.67) * mm, "radius": 1.5 * mm});
            skLineSegment(sketch, "E338", {"start": v(-9.11, 34.02) * mm, "end": v(-7.11, 32.02) * mm});
            skLineSegment(sketch, "E339", {"start": v(-9.82, 33.32) * mm, "end": v(-7.82, 31.32) * mm});
            skLineSegment(sketch, "E340", {"start": v(-7.82, 34.02) * mm, "end": v(-9.82, 32.02) * mm});
            skLineSegment(sketch, "E341", {"start": v(-7.11, 33.32) * mm, "end": v(-9.11, 31.32) * mm});
            skCircle(sketch, "E342", {"center": v(-7.96, 37.73) * mm, "radius": 1.5 * mm});
            skLineSegment(sketch, "E343", {"start": v(-8.6, 39.08) * mm, "end": v(-6.6, 37.08) * mm});
            skLineSegment(sketch, "E344", {"start": v(-9.31, 38.38) * mm, "end": v(-7.31, 36.38) * mm});
            skLineSegment(sketch, "E345", {"start": v(-7.31, 39.08) * mm, "end": v(-9.31, 37.08) * mm});
            skLineSegment(sketch, "E346", {"start": v(-6.6, 38.38) * mm, "end": v(-8.6, 36.38) * mm});
            skCircle(sketch, "E347", {"center": v(-0.3, 38.1) * mm, "radius": 1.5 * mm});
            skLineSegment(sketch, "E348", {"start": v(-0.95, 39.46) * mm, "end": v(1.05, 37.46) * mm});
            skLineSegment(sketch, "E349", {"start": v(-1.65, 38.75) * mm, "end": v(0.35, 36.75) * mm});
            skLineSegment(sketch, "E350", {"start": v(0.35, 39.46) * mm, "end": v(-1.65, 37.46) * mm});
            skLineSegment(sketch, "E351", {"start": v(1.05, 38.75) * mm, "end": v(-0.95, 36.75) * mm});
            skCircle(sketch, "E352", {"center": v(8.74, 37.98) * mm, "radius": 1.5 * mm});
            skLineSegment(sketch, "E353", {"start": v(8.1, 39.34) * mm, "end": v(10.1, 37.34) * mm});
            skLineSegment(sketch, "E354", {"start": v(7.39, 38.63) * mm, "end": v(9.39, 36.63) * mm});
            skLineSegment(sketch, "E355", {"start": v(9.39, 39.34) * mm, "end": v(7.39, 37.34) * mm});
            skLineSegment(sketch, "E356", {"start": v(10.1, 38.63) * mm, "end": v(8.1, 36.63) * mm});
            skCircle(sketch, "E357", {"center": v(9.62, 43) * mm, "radius": 1.5 * mm});
            skLineSegment(sketch, "E358", {"start": v(8.97, 44.36) * mm, "end": v(10.97, 42.36) * mm});
            skLineSegment(sketch, "E359", {"start": v(8.27, 43.65) * mm, "end": v(10.27, 41.65) * mm});
            skLineSegment(sketch, "E360", {"start": v(10.27, 44.36) * mm, "end": v(8.27, 42.36) * mm});
            skLineSegment(sketch, "E361", {"start": v(10.97, 43.65) * mm, "end": v(8.97, 41.65) * mm});
            skCircle(sketch, "E362", {"center": v(2.59, 42.75) * mm, "radius": 1.5 * mm});
            skLineSegment(sketch, "E363", {"start": v(1.94, 44.1) * mm, "end": v(3.94, 42.1) * mm});
            skLineSegment(sketch, "E364", {"start": v(1.23, 43.4) * mm, "end": v(3.23, 41.4) * mm});
            skLineSegment(sketch, "E365", {"start": v(3.23, 44.1) * mm, "end": v(1.23, 42.1) * mm});
            skLineSegment(sketch, "E366", {"start": v(3.94, 43.4) * mm, "end": v(1.94, 41.4) * mm});
            skCircle(sketch, "E367", {"center": v(-8.46, 43.5) * mm, "radius": 1.5 * mm});
            skLineSegment(sketch, "E368", {"start": v(-9.1, 44.86) * mm, "end": v(-7.1, 42.86) * mm});
            skLineSegment(sketch, "E369", {"start": v(-9.82, 44.15) * mm, "end": v(-7.82, 42.15) * mm});
            skLineSegment(sketch, "E370", {"start": v(-7.82, 44.86) * mm, "end": v(-9.82, 42.86) * mm});
            skLineSegment(sketch, "E371", {"start": v(-7.1, 44.15) * mm, "end": v(-9.1, 42.15) * mm});
            skCircle(sketch, "E372", {"center": v(-8.34, 48.15) * mm, "radius": 1.5 * mm});
            skLineSegment(sketch, "E373", {"start": v(-8.98, 49.5) * mm, "end": v(-6.98, 47.5) * mm});
            skLineSegment(sketch, "E374", {"start": v(-9.7, 48.8) * mm, "end": v(-7.7, 46.8) * mm});
            skLineSegment(sketch, "E375", {"start": v(-7.7, 49.5) * mm, "end": v(-9.7, 47.5) * mm});
            skLineSegment(sketch, "E376", {"start": v(-6.98, 48.8) * mm, "end": v(-8.98, 46.8) * mm});
            skCircle(sketch, "E377", {"center": v(0.58, 47.78) * mm, "radius": 1.5 * mm});
            skLineSegment(sketch, "E378", {"start": v(-0.07, 49.13) * mm, "end": v(1.93, 47.13) * mm});
            skLineSegment(sketch, "E379", {"start": v(-0.77, 48.42) * mm, "end": v(1.23, 46.42) * mm});
            skLineSegment(sketch, "E380", {"start": v(1.23, 49.13) * mm, "end": v(-0.77, 47.13) * mm});
            skLineSegment(sketch, "E381", {"start": v(1.93, 48.42) * mm, "end": v(-0.07, 46.42) * mm});
            skCircle(sketch, "E382", {"center": v(8.62, 48.03) * mm, "radius": 1.5 * mm});
            skLineSegment(sketch, "E383", {"start": v(7.97, 49.38) * mm, "end": v(9.97, 47.38) * mm});
            skLineSegment(sketch, "E384", {"start": v(7.26, 48.67) * mm, "end": v(9.26, 46.67) * mm});
            skLineSegment(sketch, "E385", {"start": v(9.26, 49.38) * mm, "end": v(7.26, 47.38) * mm});
            skLineSegment(sketch, "E386", {"start": v(9.97, 48.67) * mm, "end": v(7.97, 46.67) * mm});
            skCircle(sketch, "E387", {"center": v(8.87, 52.3) * mm, "radius": 1.5 * mm});
            skLineSegment(sketch, "E388", {"start": v(8.22, 53.65) * mm, "end": v(10.22, 51.65) * mm});
            skLineSegment(sketch, "E389", {"start": v(7.51, 52.94) * mm, "end": v(9.51, 50.94) * mm});
            skLineSegment(sketch, "E390", {"start": v(9.51, 53.65) * mm, "end": v(7.51, 51.65) * mm});
            skLineSegment(sketch, "E391", {"start": v(10.22, 52.94) * mm, "end": v(8.22, 50.94) * mm});
            skCircle(sketch, "E392", {"center": v(0.58, 52.55) * mm, "radius": 1.5 * mm});
            skLineSegment(sketch, "E393", {"start": v(-0.07, 53.9) * mm, "end": v(1.93, 51.9) * mm});
            skLineSegment(sketch, "E394", {"start": v(-0.77, 53.2) * mm, "end": v(1.23, 51.2) * mm});
            skLineSegment(sketch, "E395", {"start": v(1.23, 53.9) * mm, "end": v(-0.77, 51.9) * mm});
            skLineSegment(sketch, "E396", {"start": v(1.93, 53.2) * mm, "end": v(-0.07, 51.2) * mm});
            skCircle(sketch, "E397", {"center": v(-8.21, 53.05) * mm, "radius": 1.5 * mm});
            skLineSegment(sketch, "E398", {"start": v(-8.86, 54.4) * mm, "end": v(-6.86, 52.4) * mm});
            skLineSegment(sketch, "E399", {"start": v(-9.56, 53.7) * mm, "end": v(-7.56, 51.7) * mm});
            skLineSegment(sketch, "E400", {"start": v(-7.56, 54.4) * mm, "end": v(-9.56, 52.4) * mm});
            skLineSegment(sketch, "E401", {"start": v(-6.86, 53.7) * mm, "end": v(-8.86, 51.7) * mm});
            skCircle(sketch, "E402", {"center": v(-7.96, 58.07) * mm, "radius": 1.5 * mm});
            skLineSegment(sketch, "E403", {"start": v(-8.6, 59.43) * mm, "end": v(-6.6, 57.43) * mm});
            skLineSegment(sketch, "E404", {"start": v(-9.31, 58.72) * mm, "end": v(-7.31, 56.72) * mm});
            skLineSegment(sketch, "E405", {"start": v(-7.31, 59.43) * mm, "end": v(-9.31, 57.43) * mm});
            skLineSegment(sketch, "E406", {"start": v(-6.6, 58.72) * mm, "end": v(-8.6, 56.72) * mm});
            skCircle(sketch, "E407", {"center": v(0.58, 58.2) * mm, "radius": 1.5 * mm});
            skLineSegment(sketch, "E408", {"start": v(-0.07, 59.55) * mm, "end": v(1.93, 57.55) * mm});
            skLineSegment(sketch, "E409", {"start": v(-0.77, 58.85) * mm, "end": v(1.23, 56.85) * mm});
            skLineSegment(sketch, "E410", {"start": v(1.23, 59.55) * mm, "end": v(-0.77, 57.55) * mm});
            skLineSegment(sketch, "E411", {"start": v(1.93, 58.85) * mm, "end": v(-0.07, 56.85) * mm});
            skCircle(sketch, "E412", {"center": v(9.12, 57.82) * mm, "radius": 1.5 * mm});
            skLineSegment(sketch, "E413", {"start": v(8.47, 59.18) * mm, "end": v(10.47, 57.18) * mm});
            skLineSegment(sketch, "E414", {"start": v(7.76, 58.47) * mm, "end": v(9.76, 56.47) * mm});
            skLineSegment(sketch, "E415", {"start": v(9.76, 59.18) * mm, "end": v(7.76, 57.18) * mm});
            skLineSegment(sketch, "E416", {"start": v(10.47, 58.47) * mm, "end": v(8.47, 56.47) * mm});
            skCircle(sketch, "E417", {"center": v(9.12, 62.6) * mm, "radius": 1.5 * mm});
            skLineSegment(sketch, "E418", {"start": v(8.47, 63.95) * mm, "end": v(10.47, 61.95) * mm});
            skLineSegment(sketch, "E419", {"start": v(7.76, 63.24) * mm, "end": v(9.76, 61.24) * mm});
            skLineSegment(sketch, "E420", {"start": v(9.76, 63.95) * mm, "end": v(7.76, 61.95) * mm});
            skLineSegment(sketch, "E421", {"start": v(10.47, 63.24) * mm, "end": v(8.47, 61.24) * mm});
            skCircle(sketch, "E422", {"center": v(0.58, 62.34) * mm, "radius": 1.5 * mm});
            skLineSegment(sketch, "E423", {"start": v(-0.07, 63.7) * mm, "end": v(1.93, 61.7) * mm});
            skLineSegment(sketch, "E424", {"start": v(-0.77, 62.99) * mm, "end": v(1.23, 60.99) * mm});
            skLineSegment(sketch, "E425", {"start": v(1.23, 63.7) * mm, "end": v(-0.77, 61.7) * mm});
            skLineSegment(sketch, "E426", {"start": v(1.93, 62.99) * mm, "end": v(-0.07, 60.99) * mm});
            skCircle(sketch, "E427", {"center": v(-8.21, 62.85) * mm, "radius": 1.5 * mm});
            skLineSegment(sketch, "E428", {"start": v(-8.86, 64.2) * mm, "end": v(-6.86, 62.2) * mm});
            skLineSegment(sketch, "E429", {"start": v(-9.56, 63.5) * mm, "end": v(-7.56, 61.5) * mm});
            skLineSegment(sketch, "E430", {"start": v(-7.56, 64.2) * mm, "end": v(-9.56, 62.2) * mm});
            skLineSegment(sketch, "E431", {"start": v(-6.86, 63.5) * mm, "end": v(-8.86, 61.5) * mm});
            skCircle(sketch, "E432", {"center": v(-8.21, 68.12) * mm, "radius": 1.5 * mm});
            skLineSegment(sketch, "E433", {"start": v(-8.86, 69.47) * mm, "end": v(-6.86, 67.47) * mm});
            skLineSegment(sketch, "E434", {"start": v(-9.56, 68.77) * mm, "end": v(-7.56, 66.77) * mm});
            skLineSegment(sketch, "E435", {"start": v(-7.56, 69.47) * mm, "end": v(-9.56, 67.47) * mm});
            skLineSegment(sketch, "E436", {"start": v(-6.86, 68.77) * mm, "end": v(-8.86, 66.77) * mm});
            skCircle(sketch, "E437", {"center": v(-0.17, 67.11) * mm, "radius": 1.5 * mm});
            skLineSegment(sketch, "E438", {"start": v(-0.82, 68.47) * mm, "end": v(1.18, 66.47) * mm});
            skLineSegment(sketch, "E439", {"start": v(-1.53, 67.76) * mm, "end": v(0.47, 65.76) * mm});
            skLineSegment(sketch, "E440", {"start": v(0.47, 68.47) * mm, "end": v(-1.53, 66.47) * mm});
            skLineSegment(sketch, "E441", {"start": v(1.18, 67.76) * mm, "end": v(-0.82, 65.76) * mm});
            skCircle(sketch, "E442", {"center": v(8.62, 67.62) * mm, "radius": 1.5 * mm});
            skLineSegment(sketch, "E443", {"start": v(7.97, 68.97) * mm, "end": v(9.97, 66.97) * mm});
            skLineSegment(sketch, "E444", {"start": v(7.26, 68.26) * mm, "end": v(9.26, 66.26) * mm});
            skLineSegment(sketch, "E445", {"start": v(9.26, 68.97) * mm, "end": v(7.26, 66.97) * mm});
            skLineSegment(sketch, "E446", {"start": v(9.97, 68.26) * mm, "end": v(7.97, 66.26) * mm});
            skCircle(sketch, "E447", {"center": v(9.12, 73.14) * mm, "radius": 1.5 * mm});
            skLineSegment(sketch, "E448", {"start": v(8.47, 74.5) * mm, "end": v(10.47, 72.5) * mm});
            skLineSegment(sketch, "E449", {"start": v(7.76, 73.79) * mm, "end": v(9.76, 71.79) * mm});
            skLineSegment(sketch, "E450", {"start": v(9.76, 74.5) * mm, "end": v(7.76, 72.5) * mm});
            skLineSegment(sketch, "E451", {"start": v(10.47, 73.79) * mm, "end": v(8.47, 71.79) * mm});
            skCircle(sketch, "E452", {"center": v(0.58, 72.39) * mm, "radius": 1.5 * mm});
            skLineSegment(sketch, "E453", {"start": v(-0.07, 73.74) * mm, "end": v(1.93, 71.74) * mm});
            skLineSegment(sketch, "E454", {"start": v(-0.77, 73.04) * mm, "end": v(1.23, 71.04) * mm});
            skLineSegment(sketch, "E455", {"start": v(1.23, 73.74) * mm, "end": v(-0.77, 71.74) * mm});
            skLineSegment(sketch, "E456", {"start": v(1.93, 73.04) * mm, "end": v(-0.07, 71.04) * mm});
            skCircle(sketch, "E457", {"center": v(-8.34, 72.9) * mm, "radius": 1.5 * mm});
            skLineSegment(sketch, "E458", {"start": v(-8.98, 74.24) * mm, "end": v(-6.98, 72.24) * mm});
            skLineSegment(sketch, "E459", {"start": v(-9.7, 73.54) * mm, "end": v(-7.7, 71.54) * mm});
            skLineSegment(sketch, "E460", {"start": v(-7.7, 74.24) * mm, "end": v(-9.7, 72.24) * mm});
            skLineSegment(sketch, "E461", {"start": v(-6.98, 73.54) * mm, "end": v(-8.98, 71.54) * mm});
            skCircle(sketch, "E462", {"center": v(-8.37, 87.5) * mm, "radius": 1.5 * mm});
            skLineSegment(sketch, "E463", {"start": v(-9.02, 88.85) * mm, "end": v(-7.02, 86.85) * mm});
            skLineSegment(sketch, "E464", {"start": v(-9.73, 88.15) * mm, "end": v(-7.73, 86.15) * mm});
            skLineSegment(sketch, "E465", {"start": v(-7.73, 88.85) * mm, "end": v(-9.73, 86.85) * mm});
            skLineSegment(sketch, "E466", {"start": v(-7.02, 88.15) * mm, "end": v(-9.02, 86.15) * mm});
            skCircle(sketch, "E467", {"center": v(0.38, 87.5) * mm, "radius": 1.5 * mm});
            skLineSegment(sketch, "E468", {"start": v(-0.27, 88.85) * mm, "end": v(1.73, 86.85) * mm});
            skLineSegment(sketch, "E469", {"start": v(-0.98, 88.15) * mm, "end": v(1.02, 86.15) * mm});
            skLineSegment(sketch, "E470", {"start": v(1.02, 88.85) * mm, "end": v(-0.98, 86.85) * mm});
            skLineSegment(sketch, "E471", {"start": v(1.73, 88.15) * mm, "end": v(-0.27, 86.15) * mm});
            skCircle(sketch, "E472", {"center": v(9.13, 87.5) * mm, "radius": 1.5 * mm});
            skLineSegment(sketch, "E473", {"start": v(8.48, 88.85) * mm, "end": v(10.48, 86.85) * mm});
            skLineSegment(sketch, "E474", {"start": v(7.77, 88.15) * mm, "end": v(9.77, 86.15) * mm});
            skLineSegment(sketch, "E475", {"start": v(9.77, 88.85) * mm, "end": v(7.77, 86.85) * mm});
            skLineSegment(sketch, "E476", {"start": v(10.48, 88.15) * mm, "end": v(8.48, 86.15) * mm});
            skCircle(sketch, "E477", {"center": v(-8.37, 82.5) * mm, "radius": 1.5 * mm});
            skLineSegment(sketch, "E478", {"start": v(-9.02, 83.85) * mm, "end": v(-7.02, 81.85) * mm});
            skLineSegment(sketch, "E479", {"start": v(-9.73, 83.15) * mm, "end": v(-7.73, 81.15) * mm});
            skLineSegment(sketch, "E480", {"start": v(-7.73, 83.85) * mm, "end": v(-9.73, 81.85) * mm});
            skLineSegment(sketch, "E481", {"start": v(-7.02, 83.15) * mm, "end": v(-9.02, 81.15) * mm});
            skCircle(sketch, "E482", {"center": v(0.38, 82.5) * mm, "radius": 1.5 * mm});
            skLineSegment(sketch, "E483", {"start": v(-0.27, 83.85) * mm, "end": v(1.73, 81.85) * mm});
            skLineSegment(sketch, "E484", {"start": v(-0.98, 83.15) * mm, "end": v(1.02, 81.15) * mm});
            skLineSegment(sketch, "E485", {"start": v(1.02, 83.85) * mm, "end": v(-0.98, 81.85) * mm});
            skLineSegment(sketch, "E486", {"start": v(1.73, 83.15) * mm, "end": v(-0.27, 81.15) * mm});
            skCircle(sketch, "E487", {"center": v(9.13, 82.5) * mm, "radius": 1.5 * mm});
            skLineSegment(sketch, "E488", {"start": v(8.48, 83.85) * mm, "end": v(10.48, 81.85) * mm});
            skLineSegment(sketch, "E489", {"start": v(7.77, 83.15) * mm, "end": v(9.77, 81.15) * mm});
            skLineSegment(sketch, "E490", {"start": v(9.77, 83.85) * mm, "end": v(7.77, 81.85) * mm});
            skLineSegment(sketch, "E491", {"start": v(10.48, 83.15) * mm, "end": v(8.48, 81.15) * mm});
            skCircle(sketch, "E492", {"center": v(9.13, 77.5) * mm, "radius": 1.5 * mm});
            skLineSegment(sketch, "E493", {"start": v(8.48, 78.85) * mm, "end": v(10.48, 76.85) * mm});
            skLineSegment(sketch, "E494", {"start": v(7.77, 78.15) * mm, "end": v(9.77, 76.15) * mm});
            skLineSegment(sketch, "E495", {"start": v(9.77, 78.85) * mm, "end": v(7.77, 76.85) * mm});
            skLineSegment(sketch, "E496", {"start": v(10.48, 78.15) * mm, "end": v(8.48, 76.15) * mm});
            skCircle(sketch, "E497", {"center": v(0.38, 77.5) * mm, "radius": 1.5 * mm});
            skLineSegment(sketch, "E498", {"start": v(-0.27, 78.85) * mm, "end": v(1.73, 76.85) * mm});
            skLineSegment(sketch, "E499", {"start": v(-0.98, 78.15) * mm, "end": v(1.02, 76.15) * mm});
            skLineSegment(sketch, "E500", {"start": v(1.02, 78.85) * mm, "end": v(-0.98, 76.85) * mm});
            skLineSegment(sketch, "E501", {"start": v(1.73, 78.15) * mm, "end": v(-0.27, 76.15) * mm});
            skCircle(sketch, "E502", {"center": v(-8.37, 77.5) * mm, "radius": 1.5 * mm});
            skLineSegment(sketch, "E503", {"start": v(-9.02, 78.85) * mm, "end": v(-7.02, 76.85) * mm});
            skLineSegment(sketch, "E504", {"start": v(-9.73, 78.15) * mm, "end": v(-7.73, 76.15) * mm});
            skLineSegment(sketch, "E505", {"start": v(-7.73, 78.85) * mm, "end": v(-9.73, 76.85) * mm});
            skLineSegment(sketch, "E506", {"start": v(-7.02, 78.15) * mm, "end": v(-9.02, 76.15) * mm});
            skSolve(sketch);
        }
        {
            var Q0;
            {var subQ5=sQuery(id+"F0.wireOp",EDGE,"E1");var subQ7=sQuery(id+"F0.wireOp",EDGE,"E0.left");var subQ8=makeQuery(id+"F0.imprint","INTERSECT",VERTEX,{"derivedFrom":[subQ7,subQ5]});Q0=makeQuery(id+"F0.imprint","IMPRINT",FACE,{"disambiguationData":[TD([[makeQuery(id+"F0.imprint","IMPRINT",EDGE,{"disambiguationData":[TD([[subQ8,-1.0]])],"derivedFrom":subQ7}),1.0]])]});}
            var Q1;
            {var subQ0=sQuery(id+"F0.wireOp",EDGE,"E15");var subQ1=sQuery(id+"F0.wireOp",EDGE,"E0.left");var subQ2=makeQuery(id+"F0.imprint","INTERSECT",VERTEX,{"derivedFrom":[subQ1,subQ0]});Q1=makeQuery(id+"F0.imprint","IMPRINT",FACE,{"disambiguationData":[TD([[makeQuery(id+"F0.imprint","IMPRINT",EDGE,{"disambiguationData":[TD([[subQ2,-1.0]])],"derivedFrom":subQ1}),1.0]])]});}
            var Q2;
            {var subQ0=sQuery(id+"F0.wireOp",EDGE,"E16");var subQ1=sQuery(id+"F0.wireOp",EDGE,"E0.left");var subQ2=makeQuery(id+"F0.imprint","INTERSECT",VERTEX,{"derivedFrom":[subQ1,subQ0]});Q2=makeQuery(id+"F0.imprint","IMPRINT",FACE,{"disambiguationData":[TD([[makeQuery(id+"F0.imprint","IMPRINT",EDGE,{"disambiguationData":[TD([[subQ2,-1.0]])],"derivedFrom":subQ1}),1.0]])]});}
            var Q3;
            {var subQ0=sQuery(id+"F0.wireOp",EDGE,"E17");var subQ1=sQuery(id+"F0.wireOp",EDGE,"E0.left");var subQ2=makeQuery(id+"F0.imprint","INTERSECT",VERTEX,{"derivedFrom":[subQ1,subQ0]});Q3=makeQuery(id+"F0.imprint","IMPRINT",FACE,{"disambiguationData":[TD([[makeQuery(id+"F0.imprint","IMPRINT",EDGE,{"disambiguationData":[TD([[subQ2,-1.0]])],"derivedFrom":subQ1}),1.0]])]});}
            var Q4;
            {var subQ0=sQuery(id+"F0.wireOp",EDGE,"E18");var subQ1=sQuery(id+"F0.wireOp",EDGE,"E0.left");var subQ2=makeQuery(id+"F0.imprint","INTERSECT",VERTEX,{"derivedFrom":[subQ1,subQ0]});Q4=makeQuery(id+"F0.imprint","IMPRINT",FACE,{"disambiguationData":[TD([[makeQuery(id+"F0.imprint","IMPRINT",EDGE,{"disambiguationData":[TD([[subQ2,-1.0]])],"derivedFrom":subQ1}),1.0]])]});}
            var Q5;
            {var subQ0=sQuery(id+"F0.wireOp",EDGE,"E19");var subQ1=sQuery(id+"F0.wireOp",EDGE,"E0.left");var subQ2=makeQuery(id+"F0.imprint","INTERSECT",VERTEX,{"derivedFrom":[subQ1,subQ0]});Q5=makeQuery(id+"F0.imprint","IMPRINT",FACE,{"disambiguationData":[TD([[makeQuery(id+"F0.imprint","IMPRINT",EDGE,{"disambiguationData":[TD([[subQ2,-1.0]])],"derivedFrom":subQ1}),1.0]])]});}
            var Q6;
            {var subQ0=sQuery(id+"F0.wireOp",EDGE,"E20");var subQ1=sQuery(id+"F0.wireOp",EDGE,"E0.left");var subQ2=makeQuery(id+"F0.imprint","INTERSECT",VERTEX,{"derivedFrom":[subQ1,subQ0]});Q6=makeQuery(id+"F0.imprint","IMPRINT",FACE,{"disambiguationData":[TD([[makeQuery(id+"F0.imprint","IMPRINT",EDGE,{"disambiguationData":[TD([[subQ2,-1.0]])],"derivedFrom":subQ1}),1.0]])]});}
            var Q7;
            {var subQ0=sQuery(id+"F0.wireOp",EDGE,"E21");var subQ1=sQuery(id+"F0.wireOp",EDGE,"E0.left");var subQ2=makeQuery(id+"F0.imprint","INTERSECT",VERTEX,{"derivedFrom":[subQ1,subQ0]});Q7=makeQuery(id+"F0.imprint","IMPRINT",FACE,{"disambiguationData":[TD([[makeQuery(id+"F0.imprint","IMPRINT",EDGE,{"disambiguationData":[TD([[subQ2,-1.0]])],"derivedFrom":subQ1}),1.0]])]});}
            var Q8;
            {var subQ0=sQuery(id+"F0.wireOp",EDGE,"E22");var subQ1=sQuery(id+"F0.wireOp",EDGE,"E0.left");var subQ2=makeQuery(id+"F0.imprint","INTERSECT",VERTEX,{"derivedFrom":[subQ1,subQ0]});Q8=makeQuery(id+"F0.imprint","IMPRINT",FACE,{"disambiguationData":[TD([[makeQuery(id+"F0.imprint","IMPRINT",EDGE,{"disambiguationData":[TD([[subQ2,-1.0]])],"derivedFrom":subQ1}),1.0]])]});}
            var Q9;
            {var subQ0=sQuery(id+"F0.wireOp",EDGE,"E24");var subQ1=sQuery(id+"F0.wireOp",EDGE,"E0.left");var subQ2=makeQuery(id+"F0.imprint","INTERSECT",VERTEX,{"derivedFrom":[subQ1,subQ0]});Q9=makeQuery(id+"F0.imprint","IMPRINT",FACE,{"disambiguationData":[TD([[makeQuery(id+"F0.imprint","IMPRINT",EDGE,{"disambiguationData":[TD([[subQ2,-1.0]])],"derivedFrom":subQ1}),1.0]])]});}
            var Q10;
            {var subQ0=sQuery(id+"F0.wireOp",EDGE,"E23");var subQ1=sQuery(id+"F0.wireOp",EDGE,"E0.left");var subQ2=makeQuery(id+"F0.imprint","INTERSECT",VERTEX,{"derivedFrom":[subQ1,subQ0]});Q10=makeQuery(id+"F0.imprint","IMPRINT",FACE,{"disambiguationData":[TD([[makeQuery(id+"F0.imprint","IMPRINT",EDGE,{"disambiguationData":[TD([[subQ2,-1.0]])],"derivedFrom":subQ1}),1.0]])]});}
            var Q11;
            {var subQ0=sQuery(id+"F0.wireOp",EDGE,"E25");var subQ1=sQuery(id+"F0.wireOp",EDGE,"E0.left");var subQ2=makeQuery(id+"F0.imprint","INTERSECT",VERTEX,{"derivedFrom":[subQ1,subQ0]});Q11=makeQuery(id+"F0.imprint","IMPRINT",FACE,{"disambiguationData":[TD([[makeQuery(id+"F0.imprint","IMPRINT",EDGE,{"disambiguationData":[TD([[subQ2,1.0]])],"derivedFrom":subQ1}),1.0]])]});}
            var Q12;
            {var subQ0=sQuery(id+"F0.wireOp",EDGE,"E27");var subQ1=sQuery(id+"F0.wireOp",EDGE,"E0.left");var subQ2=makeQuery(id+"F0.imprint","INTERSECT",VERTEX,{"derivedFrom":[subQ1,subQ0]});Q12=makeQuery(id+"F0.imprint","IMPRINT",FACE,{"disambiguationData":[TD([[makeQuery(id+"F0.imprint","IMPRINT",EDGE,{"disambiguationData":[TD([[subQ2,-1.0]])],"derivedFrom":subQ1}),1.0]])]});}
            var Q13;
            {var subQ0=sQuery(id+"F0.wireOp",EDGE,"E26");var subQ1=sQuery(id+"F0.wireOp",EDGE,"E0.left");var subQ2=makeQuery(id+"F0.imprint","INTERSECT",VERTEX,{"derivedFrom":[subQ1,subQ0]});Q13=makeQuery(id+"F0.imprint","IMPRINT",FACE,{"disambiguationData":[TD([[makeQuery(id+"F0.imprint","IMPRINT",EDGE,{"disambiguationData":[TD([[subQ2,-1.0]])],"derivedFrom":subQ1}),1.0]])]});}
            var Q14;
            {var subQ0=sQuery(id+"F0.wireOp",EDGE,"E25");var subQ1=sQuery(id+"F0.wireOp",EDGE,"E0.left");var subQ2=makeQuery(id+"F0.imprint","INTERSECT",VERTEX,{"derivedFrom":[subQ1,subQ0]});Q14=makeQuery(id+"F0.imprint","IMPRINT",FACE,{"disambiguationData":[TD([[makeQuery(id+"F0.imprint","IMPRINT",EDGE,{"disambiguationData":[TD([[subQ2,-1.0]])],"derivedFrom":subQ1}),1.0]])]});}
            var Q15;
            {var subQ0=sQuery(id+"F0.wireOp",EDGE,"E29");var subQ1=sQuery(id+"F0.wireOp",EDGE,"E0.left");var subQ2=makeQuery(id+"F0.imprint","INTERSECT",VERTEX,{"derivedFrom":[subQ1,subQ0]});Q15=makeQuery(id+"F0.imprint","IMPRINT",FACE,{"disambiguationData":[TD([[makeQuery(id+"F0.imprint","IMPRINT",EDGE,{"disambiguationData":[TD([[subQ2,-1.0]])],"derivedFrom":subQ1}),1.0]])]});}
            var Q16;
            {var subQ0=sQuery(id+"F0.wireOp",EDGE,"E30");var subQ1=sQuery(id+"F0.wireOp",EDGE,"E0.left");var subQ2=makeQuery(id+"F0.imprint","INTERSECT",VERTEX,{"derivedFrom":[subQ1,subQ0]});Q16=makeQuery(id+"F0.imprint","IMPRINT",FACE,{"disambiguationData":[TD([[makeQuery(id+"F0.imprint","IMPRINT",EDGE,{"disambiguationData":[TD([[subQ2,-1.0]])],"derivedFrom":subQ1}),1.0]])]});}
            var Q17;
            {var subQ0=sQuery(id+"F0.wireOp",EDGE,"E31");var subQ1=sQuery(id+"F0.wireOp",EDGE,"E0.left");var subQ2=makeQuery(id+"F0.imprint","INTERSECT",VERTEX,{"derivedFrom":[subQ1,subQ0]});Q17=makeQuery(id+"F0.imprint","IMPRINT",FACE,{"disambiguationData":[TD([[makeQuery(id+"F0.imprint","IMPRINT",EDGE,{"disambiguationData":[TD([[subQ2,-1.0]])],"derivedFrom":subQ1}),1.0]])]});}
            var Q18;
            {var subQ0=sQuery(id+"F0.wireOp",EDGE,"E32");var subQ1=sQuery(id+"F0.wireOp",EDGE,"E0.left");var subQ2=makeQuery(id+"F0.imprint","INTERSECT",VERTEX,{"derivedFrom":[subQ1,subQ0]});Q18=makeQuery(id+"F0.imprint","IMPRINT",FACE,{"disambiguationData":[TD([[makeQuery(id+"F0.imprint","IMPRINT",EDGE,{"disambiguationData":[TD([[subQ2,-1.0]])],"derivedFrom":subQ1}),1.0]])]});}
            var Q19;
            {var subQ0=sQuery(id+"F0.wireOp",EDGE,"E33");var subQ1=sQuery(id+"F0.wireOp",EDGE,"E0.left");var subQ2=makeQuery(id+"F0.imprint","INTERSECT",VERTEX,{"derivedFrom":[subQ1,subQ0]});Q19=makeQuery(id+"F0.imprint","IMPRINT",FACE,{"disambiguationData":[TD([[makeQuery(id+"F0.imprint","IMPRINT",EDGE,{"disambiguationData":[TD([[subQ2,-1.0]])],"derivedFrom":subQ1}),1.0]])]});}
            var Q20;
            {var subQ0=sQuery(id+"F0.wireOp",EDGE,"E34");var subQ1=sQuery(id+"F0.wireOp",EDGE,"E0.left");var subQ2=makeQuery(id+"F0.imprint","INTERSECT",VERTEX,{"derivedFrom":[subQ1,subQ0]});Q20=makeQuery(id+"F0.imprint","IMPRINT",FACE,{"disambiguationData":[TD([[makeQuery(id+"F0.imprint","IMPRINT",EDGE,{"disambiguationData":[TD([[subQ2,-1.0]])],"derivedFrom":subQ1}),1.0]])]});}
            var Q21;
            {var subQ0=sQuery(id+"F0.wireOp",EDGE,"E35");var subQ1=sQuery(id+"F0.wireOp",EDGE,"E0.left");var subQ2=makeQuery(id+"F0.imprint","INTERSECT",VERTEX,{"derivedFrom":[subQ1,subQ0]});Q21=makeQuery(id+"F0.imprint","IMPRINT",FACE,{"disambiguationData":[TD([[makeQuery(id+"F0.imprint","IMPRINT",EDGE,{"disambiguationData":[TD([[subQ2,-1.0]])],"derivedFrom":subQ1}),1.0]])]});}
            var Q22;
            {var subQ0=sQuery(id+"F0.wireOp",EDGE,"E36");var subQ1=sQuery(id+"F0.wireOp",EDGE,"E0.left");var subQ2=makeQuery(id+"F0.imprint","INTERSECT",VERTEX,{"derivedFrom":[subQ1,subQ0]});Q22=makeQuery(id+"F0.imprint","IMPRINT",FACE,{"disambiguationData":[TD([[makeQuery(id+"F0.imprint","IMPRINT",EDGE,{"disambiguationData":[TD([[subQ2,-1.0]])],"derivedFrom":subQ1}),1.0]])]});}
            var Q23;
            {var subQ5=sQuery(id+"F0.wireOp",EDGE,"E3");var subQ6=sQuery(id+"F0.wireOp",EDGE,"E0.left");var subQ7=makeQuery(id+"F0.imprint","INTERSECT",VERTEX,{"derivedFrom":[subQ6,subQ5]});Q23=makeQuery(id+"F0.imprint","IMPRINT",FACE,{"disambiguationData":[TD([[makeQuery(id+"F0.imprint","IMPRINT",EDGE,{"disambiguationData":[TD([[subQ7,1.0]])],"derivedFrom":subQ6}),1.0]])]});}
            var Q24;
            {var subQ0=sQuery(id+"F0.wireOp",EDGE,"E38");var subQ1=sQuery(id+"F0.wireOp",EDGE,"E3");var subQ2=makeQuery(id+"F0.imprint","INTERSECT",VERTEX,{"derivedFrom":[subQ1,subQ0]});Q24=makeQuery(id+"F0.imprint","IMPRINT",FACE,{"disambiguationData":[TD([[makeQuery(id+"F0.imprint","IMPRINT",EDGE,{"disambiguationData":[TD([[subQ2,-1.0]])],"derivedFrom":subQ1}),1.0]])]});}
            var Q25;
            {var subQ0=sQuery(id+"F0.wireOp",EDGE,"E39");var subQ1=sQuery(id+"F0.wireOp",EDGE,"E3");var subQ2=makeQuery(id+"F0.imprint","INTERSECT",VERTEX,{"derivedFrom":[subQ1,subQ0]});Q25=makeQuery(id+"F0.imprint","IMPRINT",FACE,{"disambiguationData":[TD([[makeQuery(id+"F0.imprint","IMPRINT",EDGE,{"disambiguationData":[TD([[subQ2,-1.0]])],"derivedFrom":subQ1}),1.0]])]});}
            var Q26;
            {var subQ0=sQuery(id+"F0.wireOp",EDGE,"E40");var subQ1=sQuery(id+"F0.wireOp",EDGE,"E3");var subQ2=makeQuery(id+"F0.imprint","INTERSECT",VERTEX,{"derivedFrom":[subQ1,subQ0]});Q26=makeQuery(id+"F0.imprint","IMPRINT",FACE,{"disambiguationData":[TD([[makeQuery(id+"F0.imprint","IMPRINT",EDGE,{"disambiguationData":[TD([[subQ2,-1.0]])],"derivedFrom":subQ1}),1.0]])]});}
            var Q27;
            {var subQ0=sQuery(id+"F0.wireOp",EDGE,"E3");var subQ1=sQuery(id+"F0.wireOp",EDGE,"E0.top");var subQ2=makeQuery(id+"F0.imprint","INTERSECT",VERTEX,{"derivedFrom":[subQ1,subQ0]});Q27=makeQuery(id+"F0.imprint","IMPRINT",FACE,{"disambiguationData":[TD([[makeQuery(id+"F0.imprint","IMPRINT",EDGE,{"disambiguationData":[TD([[subQ2,-1.0]])],"derivedFrom":subQ1}),1.0]])]});}
            var Q28;
            {var subQ0=sQuery(id+"F0.wireOp",EDGE,"E5");var subQ1=sQuery(id+"F0.wireOp",EDGE,"E0.top");var subQ2=makeQuery(id+"F0.imprint","INTERSECT",VERTEX,{"derivedFrom":[subQ1,subQ0]});Q28=makeQuery(id+"F0.imprint","IMPRINT",FACE,{"disambiguationData":[TD([[makeQuery(id+"F0.imprint","IMPRINT",EDGE,{"disambiguationData":[TD([[subQ2,-1.0]])],"derivedFrom":subQ1}),1.0]])]});}
            var Q29;
            {var subQ0=sQuery(id+"F0.wireOp",EDGE,"E7");var subQ1=sQuery(id+"F0.wireOp",EDGE,"E0.top");var subQ2=makeQuery(id+"F0.imprint","INTERSECT",VERTEX,{"derivedFrom":[subQ1,subQ0]});Q29=makeQuery(id+"F0.imprint","IMPRINT",FACE,{"disambiguationData":[TD([[makeQuery(id+"F0.imprint","IMPRINT",EDGE,{"disambiguationData":[TD([[subQ2,-1.0]])],"derivedFrom":subQ1}),1.0]])]});}
            var Q30;
            {var subQ0=sQuery(id+"F0.wireOp",EDGE,"E9");var subQ1=sQuery(id+"F0.wireOp",EDGE,"E0.top");var subQ2=makeQuery(id+"F0.imprint","INTERSECT",VERTEX,{"derivedFrom":[subQ1,subQ0]});Q30=makeQuery(id+"F0.imprint","IMPRINT",FACE,{"disambiguationData":[TD([[makeQuery(id+"F0.imprint","IMPRINT",EDGE,{"disambiguationData":[TD([[subQ2,-1.0]])],"derivedFrom":subQ1}),1.0]])]});}
            var Q31;
            {var subQ0=sQuery(id+"F0.wireOp",EDGE,"E4");var subQ1=sQuery(id+"F0.wireOp",EDGE,"E0.top");var subQ2=makeQuery(id+"F0.imprint","INTERSECT",VERTEX,{"derivedFrom":[subQ1,subQ0]});Q31=makeQuery(id+"F0.imprint","IMPRINT",FACE,{"disambiguationData":[TD([[makeQuery(id+"F0.imprint","IMPRINT",EDGE,{"disambiguationData":[TD([[subQ2,1.0]])],"derivedFrom":subQ1}),1.0]])]});}
            var Q32;
            {var subQ0=sQuery(id+"F0.wireOp",EDGE,"E41");var subQ1=sQuery(id+"F0.wireOp",EDGE,"E4");var subQ2=makeQuery(id+"F0.imprint","INTERSECT",VERTEX,{"derivedFrom":[subQ1,subQ0]});Q32=makeQuery(id+"F0.imprint","IMPRINT",FACE,{"disambiguationData":[TD([[makeQuery(id+"F0.imprint","IMPRINT",EDGE,{"disambiguationData":[TD([[subQ2,-1.0]])],"derivedFrom":subQ1}),1.0]])]});}
            var Q33;
            {var subQ0=sQuery(id+"F0.wireOp",EDGE,"E40");var subQ1=sQuery(id+"F0.wireOp",EDGE,"E4");var subQ2=makeQuery(id+"F0.imprint","INTERSECT",VERTEX,{"derivedFrom":[subQ1,subQ0]});Q33=makeQuery(id+"F0.imprint","IMPRINT",FACE,{"disambiguationData":[TD([[makeQuery(id+"F0.imprint","IMPRINT",EDGE,{"disambiguationData":[TD([[subQ2,-1.0]])],"derivedFrom":subQ1}),1.0]])]});}
            var Q34;
            {var subQ0=sQuery(id+"F0.wireOp",EDGE,"E39");var subQ1=sQuery(id+"F0.wireOp",EDGE,"E4");var subQ2=makeQuery(id+"F0.imprint","INTERSECT",VERTEX,{"derivedFrom":[subQ1,subQ0]});Q34=makeQuery(id+"F0.imprint","IMPRINT",FACE,{"disambiguationData":[TD([[makeQuery(id+"F0.imprint","IMPRINT",EDGE,{"disambiguationData":[TD([[subQ2,-1.0]])],"derivedFrom":subQ1}),1.0]])]});}
            var Q35;
            {var subQ1=sQuery(id+"F0.wireOp",EDGE,"E0.right");var subQ7=sQuery(id+"F0.wireOp",EDGE,"E4");var subQ8=makeQuery(id+"F0.imprint","INTERSECT",VERTEX,{"derivedFrom":[subQ1,subQ7]});Q35=makeQuery(id+"F0.imprint","IMPRINT",FACE,{"disambiguationData":[TD([[makeQuery(id+"F0.imprint","IMPRINT",EDGE,{"disambiguationData":[TD([[subQ8,1.0]])],"derivedFrom":subQ1}),-1.0]])]});}
            var Q36;
            {var subQ0=sQuery(id+"F0.wireOp",EDGE,"E36");var subQ1=sQuery(id+"F0.wireOp",EDGE,"E0.right");var subQ2=makeQuery(id+"F0.imprint","INTERSECT",VERTEX,{"derivedFrom":[subQ1,subQ0]});Q36=makeQuery(id+"F0.imprint","IMPRINT",FACE,{"disambiguationData":[TD([[makeQuery(id+"F0.imprint","IMPRINT",EDGE,{"disambiguationData":[TD([[subQ2,-1.0]])],"derivedFrom":subQ1}),-1.0]])]});}
            var Q37;
            {var subQ0=sQuery(id+"F0.wireOp",EDGE,"E35");var subQ1=sQuery(id+"F0.wireOp",EDGE,"E0.right");var subQ2=makeQuery(id+"F0.imprint","INTERSECT",VERTEX,{"derivedFrom":[subQ1,subQ0]});Q37=makeQuery(id+"F0.imprint","IMPRINT",FACE,{"disambiguationData":[TD([[makeQuery(id+"F0.imprint","IMPRINT",EDGE,{"disambiguationData":[TD([[subQ2,-1.0]])],"derivedFrom":subQ1}),-1.0]])]});}
            var Q38;
            {var subQ0=sQuery(id+"F0.wireOp",EDGE,"E34");var subQ1=sQuery(id+"F0.wireOp",EDGE,"E0.right");var subQ2=makeQuery(id+"F0.imprint","INTERSECT",VERTEX,{"derivedFrom":[subQ1,subQ0]});Q38=makeQuery(id+"F0.imprint","IMPRINT",FACE,{"disambiguationData":[TD([[makeQuery(id+"F0.imprint","IMPRINT",EDGE,{"disambiguationData":[TD([[subQ2,-1.0]])],"derivedFrom":subQ1}),-1.0]])]});}
            var Q39;
            {var subQ0=sQuery(id+"F0.wireOp",EDGE,"E33");var subQ1=sQuery(id+"F0.wireOp",EDGE,"E0.right");var subQ2=makeQuery(id+"F0.imprint","INTERSECT",VERTEX,{"derivedFrom":[subQ1,subQ0]});Q39=makeQuery(id+"F0.imprint","IMPRINT",FACE,{"disambiguationData":[TD([[makeQuery(id+"F0.imprint","IMPRINT",EDGE,{"disambiguationData":[TD([[subQ2,-1.0]])],"derivedFrom":subQ1}),-1.0]])]});}
            var Q40;
            {var subQ0=sQuery(id+"F0.wireOp",EDGE,"E32");var subQ1=sQuery(id+"F0.wireOp",EDGE,"E0.right");var subQ2=makeQuery(id+"F0.imprint","INTERSECT",VERTEX,{"derivedFrom":[subQ1,subQ0]});Q40=makeQuery(id+"F0.imprint","IMPRINT",FACE,{"disambiguationData":[TD([[makeQuery(id+"F0.imprint","IMPRINT",EDGE,{"disambiguationData":[TD([[subQ2,-1.0]])],"derivedFrom":subQ1}),-1.0]])]});}
            var Q41;
            {var subQ0=sQuery(id+"F0.wireOp",EDGE,"E31");var subQ1=sQuery(id+"F0.wireOp",EDGE,"E0.right");var subQ2=makeQuery(id+"F0.imprint","INTERSECT",VERTEX,{"derivedFrom":[subQ1,subQ0]});Q41=makeQuery(id+"F0.imprint","IMPRINT",FACE,{"disambiguationData":[TD([[makeQuery(id+"F0.imprint","IMPRINT",EDGE,{"disambiguationData":[TD([[subQ2,-1.0]])],"derivedFrom":subQ1}),-1.0]])]});}
            var Q42;
            {var subQ0=sQuery(id+"F0.wireOp",EDGE,"E30");var subQ1=sQuery(id+"F0.wireOp",EDGE,"E0.right");var subQ2=makeQuery(id+"F0.imprint","INTERSECT",VERTEX,{"derivedFrom":[subQ1,subQ0]});Q42=makeQuery(id+"F0.imprint","IMPRINT",FACE,{"disambiguationData":[TD([[makeQuery(id+"F0.imprint","IMPRINT",EDGE,{"disambiguationData":[TD([[subQ2,-1.0]])],"derivedFrom":subQ1}),-1.0]])]});}
            var Q43;
            {var subQ0=sQuery(id+"F0.wireOp",EDGE,"E29");var subQ1=sQuery(id+"F0.wireOp",EDGE,"E0.right");var subQ2=makeQuery(id+"F0.imprint","INTERSECT",VERTEX,{"derivedFrom":[subQ1,subQ0]});Q43=makeQuery(id+"F0.imprint","IMPRINT",FACE,{"disambiguationData":[TD([[makeQuery(id+"F0.imprint","IMPRINT",EDGE,{"disambiguationData":[TD([[subQ2,-1.0]])],"derivedFrom":subQ1}),-1.0]])]});}
            var Q44;
            {var subQ0=sQuery(id+"F0.wireOp",EDGE,"E27");var subQ1=sQuery(id+"F0.wireOp",EDGE,"E0.right");var subQ2=makeQuery(id+"F0.imprint","INTERSECT",VERTEX,{"derivedFrom":[subQ1,subQ0]});Q44=makeQuery(id+"F0.imprint","IMPRINT",FACE,{"disambiguationData":[TD([[makeQuery(id+"F0.imprint","IMPRINT",EDGE,{"disambiguationData":[TD([[subQ2,-1.0]])],"derivedFrom":subQ1}),-1.0]])]});}
            var Q45;
            {var subQ0=sQuery(id+"F0.wireOp",EDGE,"E26");var subQ1=sQuery(id+"F0.wireOp",EDGE,"E0.right");var subQ2=makeQuery(id+"F0.imprint","INTERSECT",VERTEX,{"derivedFrom":[subQ1,subQ0]});Q45=makeQuery(id+"F0.imprint","IMPRINT",FACE,{"disambiguationData":[TD([[makeQuery(id+"F0.imprint","IMPRINT",EDGE,{"disambiguationData":[TD([[subQ2,-1.0]])],"derivedFrom":subQ1}),-1.0]])]});}
            var Q46;
            {var subQ0=sQuery(id+"F0.wireOp",EDGE,"E25");var subQ1=sQuery(id+"F0.wireOp",EDGE,"E0.right");var subQ2=makeQuery(id+"F0.imprint","INTERSECT",VERTEX,{"derivedFrom":[subQ1,subQ0]});Q46=makeQuery(id+"F0.imprint","IMPRINT",FACE,{"disambiguationData":[TD([[makeQuery(id+"F0.imprint","IMPRINT",EDGE,{"disambiguationData":[TD([[subQ2,1.0]])],"derivedFrom":subQ1}),-1.0]])]});}
            var Q47;
            {var subQ0=sQuery(id+"F0.wireOp",EDGE,"E24");var subQ1=sQuery(id+"F0.wireOp",EDGE,"E0.right");var subQ2=makeQuery(id+"F0.imprint","INTERSECT",VERTEX,{"derivedFrom":[subQ1,subQ0]});Q47=makeQuery(id+"F0.imprint","IMPRINT",FACE,{"disambiguationData":[TD([[makeQuery(id+"F0.imprint","IMPRINT",EDGE,{"disambiguationData":[TD([[subQ2,-1.0]])],"derivedFrom":subQ1}),-1.0]])]});}
            var Q48;
            {var subQ0=sQuery(id+"F0.wireOp",EDGE,"E23");var subQ1=sQuery(id+"F0.wireOp",EDGE,"E0.right");var subQ2=makeQuery(id+"F0.imprint","INTERSECT",VERTEX,{"derivedFrom":[subQ1,subQ0]});Q48=makeQuery(id+"F0.imprint","IMPRINT",FACE,{"disambiguationData":[TD([[makeQuery(id+"F0.imprint","IMPRINT",EDGE,{"disambiguationData":[TD([[subQ2,-1.0]])],"derivedFrom":subQ1}),-1.0]])]});}
            var Q49;
            {var subQ0=sQuery(id+"F0.wireOp",EDGE,"E22");var subQ1=sQuery(id+"F0.wireOp",EDGE,"E0.right");var subQ2=makeQuery(id+"F0.imprint","INTERSECT",VERTEX,{"derivedFrom":[subQ1,subQ0]});Q49=makeQuery(id+"F0.imprint","IMPRINT",FACE,{"disambiguationData":[TD([[makeQuery(id+"F0.imprint","IMPRINT",EDGE,{"disambiguationData":[TD([[subQ2,-1.0]])],"derivedFrom":subQ1}),-1.0]])]});}
            var Q50;
            {var subQ0=sQuery(id+"F0.wireOp",EDGE,"E25");var subQ1=sQuery(id+"F0.wireOp",EDGE,"E0.right");var subQ2=makeQuery(id+"F0.imprint","INTERSECT",VERTEX,{"derivedFrom":[subQ1,subQ0]});Q50=makeQuery(id+"F0.imprint","IMPRINT",FACE,{"disambiguationData":[TD([[makeQuery(id+"F0.imprint","IMPRINT",EDGE,{"disambiguationData":[TD([[subQ2,-1.0]])],"derivedFrom":subQ1}),-1.0]])]});}
            var Q51;
            {var subQ0=sQuery(id+"F0.wireOp",EDGE,"E20");var subQ1=sQuery(id+"F0.wireOp",EDGE,"E0.right");var subQ2=makeQuery(id+"F0.imprint","INTERSECT",VERTEX,{"derivedFrom":[subQ1,subQ0]});Q51=makeQuery(id+"F0.imprint","IMPRINT",FACE,{"disambiguationData":[TD([[makeQuery(id+"F0.imprint","IMPRINT",EDGE,{"disambiguationData":[TD([[subQ2,-1.0]])],"derivedFrom":subQ1}),-1.0]])]});}
            var Q52;
            {var subQ0=sQuery(id+"F0.wireOp",EDGE,"E19");var subQ1=sQuery(id+"F0.wireOp",EDGE,"E0.right");var subQ2=makeQuery(id+"F0.imprint","INTERSECT",VERTEX,{"derivedFrom":[subQ1,subQ0]});Q52=makeQuery(id+"F0.imprint","IMPRINT",FACE,{"disambiguationData":[TD([[makeQuery(id+"F0.imprint","IMPRINT",EDGE,{"disambiguationData":[TD([[subQ2,-1.0]])],"derivedFrom":subQ1}),-1.0]])]});}
            var Q53;
            {var subQ0=sQuery(id+"F0.wireOp",EDGE,"E18");var subQ1=sQuery(id+"F0.wireOp",EDGE,"E0.right");var subQ2=makeQuery(id+"F0.imprint","INTERSECT",VERTEX,{"derivedFrom":[subQ1,subQ0]});Q53=makeQuery(id+"F0.imprint","IMPRINT",FACE,{"disambiguationData":[TD([[makeQuery(id+"F0.imprint","IMPRINT",EDGE,{"disambiguationData":[TD([[subQ2,-1.0]])],"derivedFrom":subQ1}),-1.0]])]});}
            var Q54;
            {var subQ0=sQuery(id+"F0.wireOp",EDGE,"E21");var subQ1=sQuery(id+"F0.wireOp",EDGE,"E0.right");var subQ2=makeQuery(id+"F0.imprint","INTERSECT",VERTEX,{"derivedFrom":[subQ1,subQ0]});Q54=makeQuery(id+"F0.imprint","IMPRINT",FACE,{"disambiguationData":[TD([[makeQuery(id+"F0.imprint","IMPRINT",EDGE,{"disambiguationData":[TD([[subQ2,-1.0]])],"derivedFrom":subQ1}),-1.0]])]});}
            var Q55;
            {var subQ0=sQuery(id+"F0.wireOp",EDGE,"E17");var subQ1=sQuery(id+"F0.wireOp",EDGE,"E0.right");var subQ2=makeQuery(id+"F0.imprint","INTERSECT",VERTEX,{"derivedFrom":[subQ1,subQ0]});Q55=makeQuery(id+"F0.imprint","IMPRINT",FACE,{"disambiguationData":[TD([[makeQuery(id+"F0.imprint","IMPRINT",EDGE,{"disambiguationData":[TD([[subQ2,-1.0]])],"derivedFrom":subQ1}),-1.0]])]});}
            var Q56;
            {var subQ0=sQuery(id+"F0.wireOp",EDGE,"E16");var subQ1=sQuery(id+"F0.wireOp",EDGE,"E0.right");var subQ2=makeQuery(id+"F0.imprint","INTERSECT",VERTEX,{"derivedFrom":[subQ1,subQ0]});Q56=makeQuery(id+"F0.imprint","IMPRINT",FACE,{"disambiguationData":[TD([[makeQuery(id+"F0.imprint","IMPRINT",EDGE,{"disambiguationData":[TD([[subQ2,-1.0]])],"derivedFrom":subQ1}),-1.0]])]});}
            var Q57;
            {var subQ0=sQuery(id+"F0.wireOp",EDGE,"E15");var subQ1=sQuery(id+"F0.wireOp",EDGE,"E0.right");var subQ2=makeQuery(id+"F0.imprint","INTERSECT",VERTEX,{"derivedFrom":[subQ1,subQ0]});Q57=makeQuery(id+"F0.imprint","IMPRINT",FACE,{"disambiguationData":[TD([[makeQuery(id+"F0.imprint","IMPRINT",EDGE,{"disambiguationData":[TD([[subQ2,-1.0]])],"derivedFrom":subQ1}),-1.0]])]});}
            var Q58;
            {var subQ0=sQuery(id+"F0.wireOp",EDGE,"E14");var subQ1=sQuery(id+"F0.wireOp",EDGE,"E2");var subQ2=makeQuery(id+"F0.imprint","INTERSECT",VERTEX,{"derivedFrom":[subQ1,subQ0]});Q58=makeQuery(id+"F0.imprint","IMPRINT",FACE,{"disambiguationData":[TD([[makeQuery(id+"F0.imprint","IMPRINT",EDGE,{"disambiguationData":[TD([[subQ2,1.0]])],"derivedFrom":subQ1}),-1.0]])]});}
            var Q59;
            {var subQ5=sQuery(id+"F0.wireOp",EDGE,"E2");var subQ6=sQuery(id+"F0.wireOp",EDGE,"E0.right");var subQ7=makeQuery(id+"F0.imprint","INTERSECT",VERTEX,{"derivedFrom":[subQ6,subQ5]});Q59=makeQuery(id+"F0.imprint","IMPRINT",FACE,{"disambiguationData":[TD([[makeQuery(id+"F0.imprint","IMPRINT",EDGE,{"disambiguationData":[TD([[subQ7,-1.0]])],"derivedFrom":subQ6}),-1.0]])]});}
            var Q60;
            {var subQ0=sQuery(id+"F0.wireOp",EDGE,"E14");var subQ1=sQuery(id+"F0.wireOp",EDGE,"E1");var subQ2=makeQuery(id+"F0.imprint","INTERSECT",VERTEX,{"derivedFrom":[subQ1,subQ0]});Q60=makeQuery(id+"F0.imprint","IMPRINT",FACE,{"disambiguationData":[TD([[makeQuery(id+"F0.imprint","IMPRINT",EDGE,{"disambiguationData":[TD([[subQ2,-1.0]])],"derivedFrom":subQ1}),-1.0]])]});}
            var Q61;
            {var subQ0=sQuery(id+"F0.wireOp",EDGE,"E13");var subQ1=sQuery(id+"F0.wireOp",EDGE,"E1");var subQ2=makeQuery(id+"F0.imprint","INTERSECT",VERTEX,{"derivedFrom":[subQ1,subQ0]});Q61=makeQuery(id+"F0.imprint","IMPRINT",FACE,{"disambiguationData":[TD([[makeQuery(id+"F0.imprint","IMPRINT",EDGE,{"disambiguationData":[TD([[subQ2,-1.0]])],"derivedFrom":subQ1}),-1.0]])]});}
            var Q62;
            {var subQ0=sQuery(id+"F0.wireOp",EDGE,"E12");var subQ1=sQuery(id+"F0.wireOp",EDGE,"E1");var subQ2=makeQuery(id+"F0.imprint","INTERSECT",VERTEX,{"derivedFrom":[subQ1,subQ0]});Q62=makeQuery(id+"F0.imprint","IMPRINT",FACE,{"disambiguationData":[TD([[makeQuery(id+"F0.imprint","IMPRINT",EDGE,{"disambiguationData":[TD([[subQ2,-1.0]])],"derivedFrom":subQ1}),-1.0]])]});}
            var Q63;
            {var subQ0=sQuery(id+"F0.wireOp",EDGE,"E1");var subQ1=sQuery(id+"F0.wireOp",EDGE,"E0.bottom");var subQ2=makeQuery(id+"F0.imprint","INTERSECT",VERTEX,{"derivedFrom":[subQ1,subQ0]});Q63=makeQuery(id+"F0.imprint","IMPRINT",FACE,{"disambiguationData":[TD([[makeQuery(id+"F0.imprint","IMPRINT",EDGE,{"disambiguationData":[TD([[subQ2,-1.0]])],"derivedFrom":subQ1}),-1.0]])]});}
            var Q64;
            {var subQ0=sQuery(id+"F0.wireOp",EDGE,"E2");var subQ1=sQuery(id+"F0.wireOp",EDGE,"E0.bottom");var subQ2=makeQuery(id+"F0.imprint","INTERSECT",VERTEX,{"derivedFrom":[subQ1,subQ0]});Q64=makeQuery(id+"F0.imprint","IMPRINT",FACE,{"disambiguationData":[TD([[makeQuery(id+"F0.imprint","IMPRINT",EDGE,{"disambiguationData":[TD([[subQ2,1.0]])],"derivedFrom":subQ1}),-1.0]])]});}
            var Q65;
            {var subQ0=sQuery(id+"F0.wireOp",EDGE,"E11");var subQ1=sQuery(id+"F0.wireOp",EDGE,"E2");var subQ2=makeQuery(id+"F0.imprint","INTERSECT",VERTEX,{"derivedFrom":[subQ1,subQ0]});Q65=makeQuery(id+"F0.imprint","IMPRINT",FACE,{"disambiguationData":[TD([[makeQuery(id+"F0.imprint","IMPRINT",EDGE,{"disambiguationData":[TD([[subQ2,-1.0]])],"derivedFrom":subQ1}),-1.0]])]});}
            var Q66;
            {var subQ0=sQuery(id+"F0.wireOp",EDGE,"E12");var subQ1=sQuery(id+"F0.wireOp",EDGE,"E2");var subQ2=makeQuery(id+"F0.imprint","INTERSECT",VERTEX,{"derivedFrom":[subQ1,subQ0]});Q66=makeQuery(id+"F0.imprint","IMPRINT",FACE,{"disambiguationData":[TD([[makeQuery(id+"F0.imprint","IMPRINT",EDGE,{"disambiguationData":[TD([[subQ2,-1.0]])],"derivedFrom":subQ1}),-1.0]])]});}
            var Q67;
            {var subQ0=sQuery(id+"F0.wireOp",EDGE,"E5");var subQ1=sQuery(id+"F0.wireOp",EDGE,"E0.bottom");var subQ2=makeQuery(id+"F0.imprint","INTERSECT",VERTEX,{"derivedFrom":[subQ1,subQ0]});Q67=makeQuery(id+"F0.imprint","IMPRINT",FACE,{"disambiguationData":[TD([[makeQuery(id+"F0.imprint","IMPRINT",EDGE,{"disambiguationData":[TD([[subQ2,-1.0]])],"derivedFrom":subQ1}),-1.0]])]});}
            var Q68;
            {var subQ0=sQuery(id+"F0.wireOp",EDGE,"E7");var subQ1=sQuery(id+"F0.wireOp",EDGE,"E0.bottom");var subQ2=makeQuery(id+"F0.imprint","INTERSECT",VERTEX,{"derivedFrom":[subQ1,subQ0]});Q68=makeQuery(id+"F0.imprint","IMPRINT",FACE,{"disambiguationData":[TD([[makeQuery(id+"F0.imprint","IMPRINT",EDGE,{"disambiguationData":[TD([[subQ2,-1.0]])],"derivedFrom":subQ1}),-1.0]])]});}
            var Q69;
            {var subQ0=sQuery(id+"F0.wireOp",EDGE,"E9");var subQ1=sQuery(id+"F0.wireOp",EDGE,"E0.bottom");var subQ2=makeQuery(id+"F0.imprint","INTERSECT",VERTEX,{"derivedFrom":[subQ1,subQ0]});Q69=makeQuery(id+"F0.imprint","IMPRINT",FACE,{"disambiguationData":[TD([[makeQuery(id+"F0.imprint","IMPRINT",EDGE,{"disambiguationData":[TD([[subQ2,-1.0]])],"derivedFrom":subQ1}),-1.0]])]});}
            var Q70;
            Q70=makeQuery(id+"F2.opChamfer","BLEND_FACE",FACE,{"disambiguationData":[OSD([sQuery(id+"F0.wireOp",EDGE,"E0.bottom")])]});
            extrude(context, id + "F1", {"entities" : qUnion([Q0, Q1, Q2, Q3, Q4, Q5, Q6, Q7, Q8, Q9, Q10, Q11, Q12, Q13, Q14, Q15, Q16, Q17, Q18, Q19, Q20, Q21, Q22, Q23, Q24, Q25, Q26, Q27, Q28, Q29, Q30, Q31, Q32, Q33, Q34, Q35, Q36, Q37, Q38, Q39, Q40, Q41, Q42, Q43, Q44, Q45, Q46, Q47, Q48, Q49, Q50, Q51, Q52, Q53, Q54, Q55, Q56, Q57, Q58, Q59, Q60, Q61, Q62, Q63, Q64, Q65, Q66, Q67, Q68, Q69, Q70]), "depth" : 3 * mm, "offsetDistance" : 25 * mm});
        }
        {
            var Q0;
            {var subQ0=sQuery(id+"F0.wireOp",EDGE,"E0.top");var subQ1=makeQuery(id+"F0.imprint","INTERSECT",VERTEX,{"derivedFrom":[subQ0,sQuery(id+"F0.wireOp",EDGE,"E5")]});Q0=makeQuery(id+"F1.opExtrude","CAP_EDGE",EDGE,{"disambiguationData":[OSD([subQ0]),TDD([makeQuery(id+"F0.imprint","IMPRINT",EDGE,{"disambiguationData":[TD([[makeQuery(id+"F0.imprint","INTERSECT",VERTEX,{"derivedFrom":[subQ0,sQuery(id+"F0.wireOp",EDGE,"E3")]}),-1.0]])],"derivedFrom":subQ0}),makeQuery(id+"F0.imprint","IMPRINT",EDGE,{"disambiguationData":[TD([[subQ1,-1.0]])],"derivedFrom":subQ0})])],"isStart":false});}
            var Q1;
            {var subQ0=sQuery(id+"F0.wireOp",EDGE,"E0.top");Q1=makeQuery(id+"F1.opExtrude","CAP_EDGE",EDGE,{"disambiguationData":[OSD([subQ0]),TDD([makeQuery(id+"F0.imprint","IMPRINT",EDGE,{"disambiguationData":[TD([[makeQuery(id+"F0.imprint","INTERSECT",VERTEX,{"derivedFrom":[subQ0,sQuery(id+"F0.wireOp",EDGE,"E7")]}),-1.0]])],"derivedFrom":subQ0})])],"isStart":false});}
            var Q2;
            {var subQ0=sQuery(id+"F0.wireOp",EDGE,"E0.top");Q2=makeQuery(id+"F1.opExtrude","CAP_EDGE",EDGE,{"disambiguationData":[OSD([subQ0]),TDD([makeQuery(id+"F0.imprint","IMPRINT",EDGE,{"disambiguationData":[TD([[makeQuery(id+"F0.imprint","INTERSECT",VERTEX,{"derivedFrom":[subQ0,sQuery(id+"F0.wireOp",EDGE,"E9")]}),-1.0]])],"derivedFrom":subQ0}),makeQuery(id+"F0.imprint","IMPRINT",EDGE,{"disambiguationData":[TD([[makeQuery(id+"F0.imprint","INTERSECT",VERTEX,{"derivedFrom":[subQ0,sQuery(id+"F0.wireOp",EDGE,"E4")]}),1.0]])],"derivedFrom":subQ0})])],"isStart":false});}
            var Q3;
            Q3=makeQuery(id+"F1.opExtrude","CAP_EDGE",EDGE,{"disambiguationData":[OSD([sQuery(id+"F0.wireOp",EDGE,"E0.left")])],"isStart":false});
            var Q4;
            Q4=makeQuery(id+"F1.opExtrude","CAP_EDGE",EDGE,{"disambiguationData":[OSD([sQuery(id+"F0.wireOp",EDGE,"E0.right")])],"isStart":false});
            var Q5;
            {var subQ0=sQuery(id+"F0.wireOp",EDGE,"E0.bottom");Q5=makeQuery(id+"F1.opExtrude","CAP_EDGE",EDGE,{"disambiguationData":[OSD([subQ0]),TDD([makeQuery(id+"F0.imprint","IMPRINT",EDGE,{"disambiguationData":[TD([[makeQuery(id+"F0.imprint","INTERSECT",VERTEX,{"derivedFrom":[subQ0,sQuery(id+"F0.wireOp",EDGE,"E9")]}),-1.0]])],"derivedFrom":subQ0}),makeQuery(id+"F0.imprint","IMPRINT",EDGE,{"disambiguationData":[TD([[makeQuery(id+"F0.imprint","INTERSECT",VERTEX,{"derivedFrom":[subQ0,sQuery(id+"F0.wireOp",EDGE,"E2")]}),1.0]])],"derivedFrom":subQ0})])],"isStart":false});}
            var Q6;
            {var subQ0=sQuery(id+"F0.wireOp",EDGE,"E0.bottom");var subQ1=makeQuery(id+"F0.imprint","INTERSECT",VERTEX,{"derivedFrom":[subQ0,sQuery(id+"F0.wireOp",EDGE,"E5")]});Q6=makeQuery(id+"F1.opExtrude","CAP_EDGE",EDGE,{"disambiguationData":[OSD([subQ0]),TDD([makeQuery(id+"F0.imprint","IMPRINT",EDGE,{"disambiguationData":[TD([[makeQuery(id+"F0.imprint","INTERSECT",VERTEX,{"derivedFrom":[subQ0,sQuery(id+"F0.wireOp",EDGE,"E1")]}),-1.0]])],"derivedFrom":subQ0}),makeQuery(id+"F0.imprint","IMPRINT",EDGE,{"disambiguationData":[TD([[subQ1,-1.0]])],"derivedFrom":subQ0})])],"isStart":false});}
            chamfer(context, id + "F2", {"entities" : qUnion([Q0, Q1, Q2, Q3, Q4, Q5, Q6]), "chamferType" : ChamferType.TWO_OFFSETS, "width1" : 5 * mm, "oppositeDirection" : false, "width2" : 2 * mm, "tangentPropagation" : true});
        }
        {
            var Q0;
            Q0=makeQuery(id+"F1.opExtrude","CAP_EDGE",EDGE,{"disambiguationData":[OSD([sQuery(id+"F0.wireOp",EDGE,"E1")])],"isStart":false});
            var Q1;
            Q1=makeQuery(id+"F1.opExtrude","CAP_EDGE",EDGE,{"disambiguationData":[OSD([sQuery(id+"F0.wireOp",EDGE,"E3")])],"isStart":false});
            var Q2;
            Q2=makeQuery(id+"F1.opExtrude","CAP_EDGE",EDGE,{"disambiguationData":[OSD([sQuery(id+"F0.wireOp",EDGE,"E4")])],"isStart":false});
            var Q3;
            Q3=makeQuery(id+"F1.opExtrude","CAP_EDGE",EDGE,{"disambiguationData":[OSD([sQuery(id+"F0.wireOp",EDGE,"E2")])],"isStart":false});
            chamfer(context, id + "F3", {"entities" : qUnion([Q0, Q1, Q2, Q3]), "chamferType" : ChamferType.TWO_OFFSETS, "width1" : 2 * mm, "oppositeDirection" : false, "width2" : 3 * mm, "tangentPropagation" : true});
        }
        {
            var Q0;
            {var subQ0=sQuery(id+"F0.wireOp",EDGE,"E464");var subQ1=sQuery(id+"F0.wireOp",EDGE,"E462");var subQ2=makeQuery(id+"F0.imprint","INTERSECT",VERTEX,{"disambiguationData":[OD(1.0)],"derivedFrom":[subQ1,subQ0]});Q0=makeQuery(id+"F0.imprint","IMPRINT",FACE,{"disambiguationData":[TD([[makeQuery(id+"F0.imprint","IMPRINT",EDGE,{"disambiguationData":[TD([[subQ2,1.0]])],"derivedFrom":subQ1}),1.0]])]});}
            var Q1;
            {var subQ0=sQuery(id+"F0.wireOp",EDGE,"E464");var subQ1=sQuery(id+"F0.wireOp",EDGE,"E462");var subQ2=makeQuery(id+"F0.imprint","INTERSECT",VERTEX,{"disambiguationData":[OD(0.0)],"derivedFrom":[subQ1,subQ0]});Q1=makeQuery(id+"F0.imprint","IMPRINT",FACE,{"disambiguationData":[TD([[makeQuery(id+"F0.imprint","IMPRINT",EDGE,{"disambiguationData":[TD([[subQ2,-1.0]])],"derivedFrom":subQ1}),1.0]])]});}
            var Q2;
            {var subQ0=sQuery(id+"F0.wireOp",EDGE,"E463");var subQ1=sQuery(id+"F0.wireOp",EDGE,"E462");var subQ2=makeQuery(id+"F0.imprint","INTERSECT",VERTEX,{"disambiguationData":[OD(0.0)],"derivedFrom":[subQ1,subQ0]});Q2=makeQuery(id+"F0.imprint","IMPRINT",FACE,{"disambiguationData":[TD([[makeQuery(id+"F0.imprint","IMPRINT",EDGE,{"disambiguationData":[TD([[subQ2,1.0]])],"derivedFrom":subQ1}),1.0]])]});}
            var Q3;
            {var subQ0=sQuery(id+"F0.wireOp",EDGE,"E463");var subQ1=sQuery(id+"F0.wireOp",EDGE,"E462");var subQ2=makeQuery(id+"F0.imprint","INTERSECT",VERTEX,{"disambiguationData":[OD(1.0)],"derivedFrom":[subQ1,subQ0]});Q3=makeQuery(id+"F0.imprint","IMPRINT",FACE,{"disambiguationData":[TD([[makeQuery(id+"F0.imprint","IMPRINT",EDGE,{"disambiguationData":[TD([[subQ2,-1.0]])],"derivedFrom":subQ1}),1.0]])]});}
            var Q4;
            {var subQ0=sQuery(id+"F0.wireOp",EDGE,"E469");var subQ1=sQuery(id+"F0.wireOp",EDGE,"E467");var subQ2=makeQuery(id+"F0.imprint","INTERSECT",VERTEX,{"disambiguationData":[OD(1.0)],"derivedFrom":[subQ1,subQ0]});Q4=makeQuery(id+"F0.imprint","IMPRINT",FACE,{"disambiguationData":[TD([[makeQuery(id+"F0.imprint","IMPRINT",EDGE,{"disambiguationData":[TD([[subQ2,1.0]])],"derivedFrom":subQ1}),1.0]])]});}
            var Q5;
            {var subQ0=sQuery(id+"F0.wireOp",EDGE,"E468");var subQ1=sQuery(id+"F0.wireOp",EDGE,"E467");var subQ2=makeQuery(id+"F0.imprint","INTERSECT",VERTEX,{"disambiguationData":[OD(0.0)],"derivedFrom":[subQ1,subQ0]});Q5=makeQuery(id+"F0.imprint","IMPRINT",FACE,{"disambiguationData":[TD([[makeQuery(id+"F0.imprint","IMPRINT",EDGE,{"disambiguationData":[TD([[subQ2,1.0]])],"derivedFrom":subQ1}),1.0]])]});}
            var Q6;
            {var subQ0=sQuery(id+"F0.wireOp",EDGE,"E469");var subQ1=sQuery(id+"F0.wireOp",EDGE,"E467");var subQ2=makeQuery(id+"F0.imprint","INTERSECT",VERTEX,{"disambiguationData":[OD(0.0)],"derivedFrom":[subQ1,subQ0]});Q6=makeQuery(id+"F0.imprint","IMPRINT",FACE,{"disambiguationData":[TD([[makeQuery(id+"F0.imprint","IMPRINT",EDGE,{"disambiguationData":[TD([[subQ2,-1.0]])],"derivedFrom":subQ1}),1.0]])]});}
            var Q7;
            {var subQ0=sQuery(id+"F0.wireOp",EDGE,"E468");var subQ1=sQuery(id+"F0.wireOp",EDGE,"E467");var subQ2=makeQuery(id+"F0.imprint","INTERSECT",VERTEX,{"disambiguationData":[OD(1.0)],"derivedFrom":[subQ1,subQ0]});Q7=makeQuery(id+"F0.imprint","IMPRINT",FACE,{"disambiguationData":[TD([[makeQuery(id+"F0.imprint","IMPRINT",EDGE,{"disambiguationData":[TD([[subQ2,-1.0]])],"derivedFrom":subQ1}),1.0]])]});}
            var Q8;
            {var subQ0=sQuery(id+"F0.wireOp",EDGE,"E474");var subQ1=sQuery(id+"F0.wireOp",EDGE,"E472");var subQ2=makeQuery(id+"F0.imprint","INTERSECT",VERTEX,{"disambiguationData":[OD(0.0)],"derivedFrom":[subQ1,subQ0]});Q8=makeQuery(id+"F0.imprint","IMPRINT",FACE,{"disambiguationData":[TD([[makeQuery(id+"F0.imprint","IMPRINT",EDGE,{"disambiguationData":[TD([[subQ2,-1.0]])],"derivedFrom":subQ1}),1.0]])]});}
            var Q9;
            {var subQ0=sQuery(id+"F0.wireOp",EDGE,"E474");var subQ1=sQuery(id+"F0.wireOp",EDGE,"E472");var subQ2=makeQuery(id+"F0.imprint","INTERSECT",VERTEX,{"disambiguationData":[OD(1.0)],"derivedFrom":[subQ1,subQ0]});Q9=makeQuery(id+"F0.imprint","IMPRINT",FACE,{"disambiguationData":[TD([[makeQuery(id+"F0.imprint","IMPRINT",EDGE,{"disambiguationData":[TD([[subQ2,1.0]])],"derivedFrom":subQ1}),1.0]])]});}
            var Q10;
            {var subQ0=sQuery(id+"F0.wireOp",EDGE,"E473");var subQ1=sQuery(id+"F0.wireOp",EDGE,"E472");var subQ2=makeQuery(id+"F0.imprint","INTERSECT",VERTEX,{"disambiguationData":[OD(1.0)],"derivedFrom":[subQ1,subQ0]});Q10=makeQuery(id+"F0.imprint","IMPRINT",FACE,{"disambiguationData":[TD([[makeQuery(id+"F0.imprint","IMPRINT",EDGE,{"disambiguationData":[TD([[subQ2,-1.0]])],"derivedFrom":subQ1}),1.0]])]});}
            var Q11;
            {var subQ0=sQuery(id+"F0.wireOp",EDGE,"E473");var subQ1=sQuery(id+"F0.wireOp",EDGE,"E472");var subQ2=makeQuery(id+"F0.imprint","INTERSECT",VERTEX,{"disambiguationData":[OD(0.0)],"derivedFrom":[subQ1,subQ0]});Q11=makeQuery(id+"F0.imprint","IMPRINT",FACE,{"disambiguationData":[TD([[makeQuery(id+"F0.imprint","IMPRINT",EDGE,{"disambiguationData":[TD([[subQ2,1.0]])],"derivedFrom":subQ1}),1.0]])]});}
            extrude(context, id + "F4", {"entities" : qUnion([Q0, Q1, Q2, Q3, Q4, Q5, Q6, Q7, Q8, Q9, Q10, Q11]), "operationType" : NewBodyOperationType.ADD, "depth" : 3 * mm, "offsetDistance" : 25 * mm});
        }
        {
            var Q0;
            {var subQ0=sQuery(id+"F0.wireOp",EDGE,"E475");var subQ1=sQuery(id+"F0.wireOp",EDGE,"E472");var subQ2=makeQuery(id+"F0.imprint","INTERSECT",VERTEX,{"disambiguationData":[OD(1.0)],"derivedFrom":[subQ1,subQ0]});Q0=makeQuery(id+"F0.imprint","IMPRINT",FACE,{"disambiguationData":[TD([[makeQuery(id+"F0.imprint","IMPRINT",EDGE,{"disambiguationData":[TD([[subQ2,-1.0]])],"derivedFrom":subQ1}),1.0]])]});}
            var Q1;
            {var subQ0=sQuery(id+"F0.wireOp",EDGE,"E473");var subQ1=sQuery(id+"F0.wireOp",EDGE,"E472");var subQ2=makeQuery(id+"F0.imprint","INTERSECT",VERTEX,{"disambiguationData":[OD(1.0)],"derivedFrom":[subQ1,subQ0]});Q1=makeQuery(id+"F0.imprint","IMPRINT",FACE,{"disambiguationData":[TD([[makeQuery(id+"F0.imprint","IMPRINT",EDGE,{"disambiguationData":[TD([[subQ2,1.0]])],"derivedFrom":subQ1}),1.0]])]});}
            var Q2;
            {var subQ0=sQuery(id+"F0.wireOp",EDGE,"E475");var subQ1=sQuery(id+"F0.wireOp",EDGE,"E473");var subQ2=makeQuery(id+"F0.imprint","INTERSECT",VERTEX,{"derivedFrom":[subQ1,subQ0]});Q2=makeQuery(id+"F0.imprint","IMPRINT",FACE,{"disambiguationData":[TD([[makeQuery(id+"F0.imprint","IMPRINT",EDGE,{"disambiguationData":[TD([[subQ2,-1.0]])],"derivedFrom":subQ1}),-1.0]])]});}
            var Q3;
            {var subQ0=sQuery(id+"F0.wireOp",EDGE,"E473");var subQ1=sQuery(id+"F0.wireOp",EDGE,"E472");var subQ2=makeQuery(id+"F0.imprint","INTERSECT",VERTEX,{"disambiguationData":[OD(0.0)],"derivedFrom":[subQ1,subQ0]});Q3=makeQuery(id+"F0.imprint","IMPRINT",FACE,{"disambiguationData":[TD([[makeQuery(id+"F0.imprint","IMPRINT",EDGE,{"disambiguationData":[TD([[subQ2,-1.0]])],"derivedFrom":subQ1}),1.0]])]});}
            var Q4;
            {var subQ0=sQuery(id+"F0.wireOp",EDGE,"E475");var subQ1=sQuery(id+"F0.wireOp",EDGE,"E472");var subQ2=makeQuery(id+"F0.imprint","INTERSECT",VERTEX,{"disambiguationData":[OD(0.0)],"derivedFrom":[subQ1,subQ0]});Q4=makeQuery(id+"F0.imprint","IMPRINT",FACE,{"disambiguationData":[TD([[makeQuery(id+"F0.imprint","IMPRINT",EDGE,{"disambiguationData":[TD([[subQ2,1.0]])],"derivedFrom":subQ1}),1.0]])]});}
            var Q5;
            {var subQ0=sQuery(id+"F0.wireOp",EDGE,"E468");var subQ1=sQuery(id+"F0.wireOp",EDGE,"E467");var subQ2=makeQuery(id+"F0.imprint","INTERSECT",VERTEX,{"disambiguationData":[OD(1.0)],"derivedFrom":[subQ1,subQ0]});Q5=makeQuery(id+"F0.imprint","IMPRINT",FACE,{"disambiguationData":[TD([[makeQuery(id+"F0.imprint","IMPRINT",EDGE,{"disambiguationData":[TD([[subQ2,1.0]])],"derivedFrom":subQ1}),1.0]])]});}
            var Q6;
            {var subQ0=sQuery(id+"F0.wireOp",EDGE,"E470");var subQ1=sQuery(id+"F0.wireOp",EDGE,"E467");var subQ2=makeQuery(id+"F0.imprint","INTERSECT",VERTEX,{"disambiguationData":[OD(1.0)],"derivedFrom":[subQ1,subQ0]});Q6=makeQuery(id+"F0.imprint","IMPRINT",FACE,{"disambiguationData":[TD([[makeQuery(id+"F0.imprint","IMPRINT",EDGE,{"disambiguationData":[TD([[subQ2,-1.0]])],"derivedFrom":subQ1}),1.0]])]});}
            var Q7;
            {var subQ0=sQuery(id+"F0.wireOp",EDGE,"E470");var subQ1=sQuery(id+"F0.wireOp",EDGE,"E468");var subQ2=makeQuery(id+"F0.imprint","INTERSECT",VERTEX,{"derivedFrom":[subQ1,subQ0]});Q7=makeQuery(id+"F0.imprint","IMPRINT",FACE,{"disambiguationData":[TD([[makeQuery(id+"F0.imprint","IMPRINT",EDGE,{"disambiguationData":[TD([[subQ2,-1.0]])],"derivedFrom":subQ1}),-1.0]])]});}
            var Q8;
            {var subQ0=sQuery(id+"F0.wireOp",EDGE,"E468");var subQ1=sQuery(id+"F0.wireOp",EDGE,"E467");var subQ2=makeQuery(id+"F0.imprint","INTERSECT",VERTEX,{"disambiguationData":[OD(0.0)],"derivedFrom":[subQ1,subQ0]});Q8=makeQuery(id+"F0.imprint","IMPRINT",FACE,{"disambiguationData":[TD([[makeQuery(id+"F0.imprint","IMPRINT",EDGE,{"disambiguationData":[TD([[subQ2,-1.0]])],"derivedFrom":subQ1}),1.0]])]});}
            var Q9;
            {var subQ0=sQuery(id+"F0.wireOp",EDGE,"E470");var subQ1=sQuery(id+"F0.wireOp",EDGE,"E467");var subQ2=makeQuery(id+"F0.imprint","INTERSECT",VERTEX,{"disambiguationData":[OD(0.0)],"derivedFrom":[subQ1,subQ0]});Q9=makeQuery(id+"F0.imprint","IMPRINT",FACE,{"disambiguationData":[TD([[makeQuery(id+"F0.imprint","IMPRINT",EDGE,{"disambiguationData":[TD([[subQ2,1.0]])],"derivedFrom":subQ1}),1.0]])]});}
            var Q10;
            {var subQ0=sQuery(id+"F0.wireOp",EDGE,"E465");var subQ1=sQuery(id+"F0.wireOp",EDGE,"E462");var subQ2=makeQuery(id+"F0.imprint","INTERSECT",VERTEX,{"disambiguationData":[OD(1.0)],"derivedFrom":[subQ1,subQ0]});Q10=makeQuery(id+"F0.imprint","IMPRINT",FACE,{"disambiguationData":[TD([[makeQuery(id+"F0.imprint","IMPRINT",EDGE,{"disambiguationData":[TD([[subQ2,-1.0]])],"derivedFrom":subQ1}),1.0]])]});}
            var Q11;
            {var subQ0=sQuery(id+"F0.wireOp",EDGE,"E465");var subQ1=sQuery(id+"F0.wireOp",EDGE,"E463");var subQ2=makeQuery(id+"F0.imprint","INTERSECT",VERTEX,{"derivedFrom":[subQ1,subQ0]});Q11=makeQuery(id+"F0.imprint","IMPRINT",FACE,{"disambiguationData":[TD([[makeQuery(id+"F0.imprint","IMPRINT",EDGE,{"disambiguationData":[TD([[subQ2,-1.0]])],"derivedFrom":subQ1}),-1.0]])]});}
            var Q12;
            {var subQ0=sQuery(id+"F0.wireOp",EDGE,"E463");var subQ1=sQuery(id+"F0.wireOp",EDGE,"E462");var subQ2=makeQuery(id+"F0.imprint","INTERSECT",VERTEX,{"disambiguationData":[OD(0.0)],"derivedFrom":[subQ1,subQ0]});Q12=makeQuery(id+"F0.imprint","IMPRINT",FACE,{"disambiguationData":[TD([[makeQuery(id+"F0.imprint","IMPRINT",EDGE,{"disambiguationData":[TD([[subQ2,-1.0]])],"derivedFrom":subQ1}),1.0]])]});}
            var Q13;
            {var subQ0=sQuery(id+"F0.wireOp",EDGE,"E463");var subQ1=sQuery(id+"F0.wireOp",EDGE,"E462");var subQ2=makeQuery(id+"F0.imprint","INTERSECT",VERTEX,{"disambiguationData":[OD(1.0)],"derivedFrom":[subQ1,subQ0]});Q13=makeQuery(id+"F0.imprint","IMPRINT",FACE,{"disambiguationData":[TD([[makeQuery(id+"F0.imprint","IMPRINT",EDGE,{"disambiguationData":[TD([[subQ2,1.0]])],"derivedFrom":subQ1}),1.0]])]});}
            var Q14;
            {var subQ0=sQuery(id+"F0.wireOp",EDGE,"E465");var subQ1=sQuery(id+"F0.wireOp",EDGE,"E462");var subQ2=makeQuery(id+"F0.imprint","INTERSECT",VERTEX,{"disambiguationData":[OD(0.0)],"derivedFrom":[subQ1,subQ0]});Q14=makeQuery(id+"F0.imprint","IMPRINT",FACE,{"disambiguationData":[TD([[makeQuery(id+"F0.imprint","IMPRINT",EDGE,{"disambiguationData":[TD([[subQ2,1.0]])],"derivedFrom":subQ1}),1.0]])]});}
            extrude(context, id + "F5", {"entities" : qUnion([Q0, Q1, Q2, Q3, Q4, Q5, Q6, Q7, Q8, Q9, Q10, Q11, Q12, Q13, Q14]), "operationType" : NewBodyOperationType.ADD, "depth" : 4 * mm, "offsetDistance" : 25 * mm});
        }
        {
            var Q0;
            {var subQ0=sQuery(id+"F0.wireOp",EDGE,"E6");var subQ1=sQuery(id+"F0.wireOp",EDGE,"E0.top");var subQ2=makeQuery(id+"F0.imprint","INTERSECT",VERTEX,{"derivedFrom":[subQ1,subQ0]});Q0=makeQuery(id+"F0.imprint","IMPRINT",FACE,{"disambiguationData":[TD([[makeQuery(id+"F0.imprint","IMPRINT",EDGE,{"disambiguationData":[TD([[subQ2,-1.0]])],"derivedFrom":subQ1}),1.0]])]});}
            var Q1;
            {var subQ0=sQuery(id+"F0.wireOp",EDGE,"E8");var subQ1=sQuery(id+"F0.wireOp",EDGE,"E0.top");var subQ2=makeQuery(id+"F0.imprint","INTERSECT",VERTEX,{"derivedFrom":[subQ1,subQ0]});Q1=makeQuery(id+"F0.imprint","IMPRINT",FACE,{"disambiguationData":[TD([[makeQuery(id+"F0.imprint","IMPRINT",EDGE,{"disambiguationData":[TD([[subQ2,-1.0]])],"derivedFrom":subQ1}),1.0]])]});}
            var Q2;
            {var subQ0=sQuery(id+"F0.wireOp",EDGE,"E6");var subQ1=sQuery(id+"F0.wireOp",EDGE,"E0.bottom");var subQ2=makeQuery(id+"F0.imprint","INTERSECT",VERTEX,{"derivedFrom":[subQ1,subQ0]});Q2=makeQuery(id+"F0.imprint","IMPRINT",FACE,{"disambiguationData":[TD([[makeQuery(id+"F0.imprint","IMPRINT",EDGE,{"disambiguationData":[TD([[subQ2,-1.0]])],"derivedFrom":subQ1}),-1.0]])]});}
            var Q3;
            {var subQ0=sQuery(id+"F0.wireOp",EDGE,"E8");var subQ1=sQuery(id+"F0.wireOp",EDGE,"E0.bottom");var subQ2=makeQuery(id+"F0.imprint","INTERSECT",VERTEX,{"derivedFrom":[subQ1,subQ0]});Q3=makeQuery(id+"F0.imprint","IMPRINT",FACE,{"disambiguationData":[TD([[makeQuery(id+"F0.imprint","IMPRINT",EDGE,{"disambiguationData":[TD([[subQ2,-1.0]])],"derivedFrom":subQ1}),-1.0]])]});}
            var Q4;
            {var subQ0=sQuery(id+"F0.wireOp",EDGE,"E11");var subQ1=sQuery(id+"F0.wireOp",EDGE,"E8");var subQ2=makeQuery(id+"F0.imprint","INTERSECT",VERTEX,{"derivedFrom":[subQ1,subQ0]});Q4=makeQuery(id+"F0.imprint","IMPRINT",FACE,{"disambiguationData":[TD([[makeQuery(id+"F0.imprint","IMPRINT",EDGE,{"disambiguationData":[TD([[subQ2,-1.0]])],"derivedFrom":subQ1}),1.0]])]});}
            var Q5;
            {var subQ0=sQuery(id+"F0.wireOp",EDGE,"E11");var subQ1=sQuery(id+"F0.wireOp",EDGE,"E6");var subQ2=makeQuery(id+"F0.imprint","INTERSECT",VERTEX,{"derivedFrom":[subQ1,subQ0]});Q5=makeQuery(id+"F0.imprint","IMPRINT",FACE,{"disambiguationData":[TD([[makeQuery(id+"F0.imprint","IMPRINT",EDGE,{"disambiguationData":[TD([[subQ2,-1.0]])],"derivedFrom":subQ1}),1.0]])]});}
            var Q6;
            {var subQ0=sQuery(id+"F0.wireOp",EDGE,"E12");var subQ1=sQuery(id+"F0.wireOp",EDGE,"E6");var subQ2=makeQuery(id+"F0.imprint","INTERSECT",VERTEX,{"derivedFrom":[subQ1,subQ0]});Q6=makeQuery(id+"F0.imprint","IMPRINT",FACE,{"disambiguationData":[TD([[makeQuery(id+"F0.imprint","IMPRINT",EDGE,{"disambiguationData":[TD([[subQ2,-1.0]])],"derivedFrom":subQ1}),1.0]])]});}
            var Q7;
            {var subQ0=sQuery(id+"F0.wireOp",EDGE,"E12");var subQ1=sQuery(id+"F0.wireOp",EDGE,"E8");var subQ2=makeQuery(id+"F0.imprint","INTERSECT",VERTEX,{"derivedFrom":[subQ1,subQ0]});Q7=makeQuery(id+"F0.imprint","IMPRINT",FACE,{"disambiguationData":[TD([[makeQuery(id+"F0.imprint","IMPRINT",EDGE,{"disambiguationData":[TD([[subQ2,-1.0]])],"derivedFrom":subQ1}),1.0]])]});}
            var Q8;
            {var subQ0=sQuery(id+"F0.wireOp",EDGE,"E40");var subQ1=sQuery(id+"F0.wireOp",EDGE,"E8");var subQ2=makeQuery(id+"F0.imprint","INTERSECT",VERTEX,{"derivedFrom":[subQ1,subQ0]});Q8=makeQuery(id+"F0.imprint","IMPRINT",FACE,{"disambiguationData":[TD([[makeQuery(id+"F0.imprint","IMPRINT",EDGE,{"disambiguationData":[TD([[subQ2,-1.0]])],"derivedFrom":subQ1}),1.0]])]});}
            var Q9;
            {var subQ0=sQuery(id+"F0.wireOp",EDGE,"E40");var subQ1=sQuery(id+"F0.wireOp",EDGE,"E6");var subQ2=makeQuery(id+"F0.imprint","INTERSECT",VERTEX,{"derivedFrom":[subQ1,subQ0]});Q9=makeQuery(id+"F0.imprint","IMPRINT",FACE,{"disambiguationData":[TD([[makeQuery(id+"F0.imprint","IMPRINT",EDGE,{"disambiguationData":[TD([[subQ2,-1.0]])],"derivedFrom":subQ1}),1.0]])]});}
            var Q10;
            {var subQ0=sQuery(id+"F0.wireOp",EDGE,"E39");var subQ1=sQuery(id+"F0.wireOp",EDGE,"E6");var subQ2=makeQuery(id+"F0.imprint","INTERSECT",VERTEX,{"derivedFrom":[subQ1,subQ0]});Q10=makeQuery(id+"F0.imprint","IMPRINT",FACE,{"disambiguationData":[TD([[makeQuery(id+"F0.imprint","IMPRINT",EDGE,{"disambiguationData":[TD([[subQ2,-1.0]])],"derivedFrom":subQ1}),1.0]])]});}
            var Q11;
            {var subQ0=sQuery(id+"F0.wireOp",EDGE,"E37");var subQ1=sQuery(id+"F0.wireOp",EDGE,"E8");var subQ2=makeQuery(id+"F0.imprint","INTERSECT",VERTEX,{"derivedFrom":[subQ1,subQ0]});Q11=makeQuery(id+"F0.imprint","IMPRINT",FACE,{"disambiguationData":[TD([[makeQuery(id+"F0.imprint","IMPRINT",EDGE,{"disambiguationData":[TD([[subQ2,-1.0]])],"derivedFrom":subQ1}),1.0]])]});}
            var Q12;
            {var subQ0=sQuery(id+"F0.wireOp",EDGE,"E36");var subQ1=sQuery(id+"F0.wireOp",EDGE,"E8");var subQ2=makeQuery(id+"F0.imprint","INTERSECT",VERTEX,{"derivedFrom":[subQ1,subQ0]});Q12=makeQuery(id+"F0.imprint","IMPRINT",FACE,{"disambiguationData":[TD([[makeQuery(id+"F0.imprint","IMPRINT",EDGE,{"disambiguationData":[TD([[subQ2,-1.0]])],"derivedFrom":subQ1}),1.0]])]});}
            var Q13;
            {var subQ0=sQuery(id+"F0.wireOp",EDGE,"E35");var subQ1=sQuery(id+"F0.wireOp",EDGE,"E8");var subQ2=makeQuery(id+"F0.imprint","INTERSECT",VERTEX,{"derivedFrom":[subQ1,subQ0]});Q13=makeQuery(id+"F0.imprint","IMPRINT",FACE,{"disambiguationData":[TD([[makeQuery(id+"F0.imprint","IMPRINT",EDGE,{"disambiguationData":[TD([[subQ2,-1.0]])],"derivedFrom":subQ1}),1.0]])]});}
            var Q14;
            {var subQ0=sQuery(id+"F0.wireOp",EDGE,"E34");var subQ1=sQuery(id+"F0.wireOp",EDGE,"E8");var subQ2=makeQuery(id+"F0.imprint","INTERSECT",VERTEX,{"derivedFrom":[subQ1,subQ0]});Q14=makeQuery(id+"F0.imprint","IMPRINT",FACE,{"disambiguationData":[TD([[makeQuery(id+"F0.imprint","IMPRINT",EDGE,{"disambiguationData":[TD([[subQ2,-1.0]])],"derivedFrom":subQ1}),1.0]])]});}
            var Q15;
            {var subQ0=sQuery(id+"F0.wireOp",EDGE,"E33");var subQ1=sQuery(id+"F0.wireOp",EDGE,"E8");var subQ2=makeQuery(id+"F0.imprint","INTERSECT",VERTEX,{"derivedFrom":[subQ1,subQ0]});Q15=makeQuery(id+"F0.imprint","IMPRINT",FACE,{"disambiguationData":[TD([[makeQuery(id+"F0.imprint","IMPRINT",EDGE,{"disambiguationData":[TD([[subQ2,-1.0]])],"derivedFrom":subQ1}),1.0]])]});}
            var Q16;
            {var subQ0=sQuery(id+"F0.wireOp",EDGE,"E32");var subQ1=sQuery(id+"F0.wireOp",EDGE,"E8");var subQ2=makeQuery(id+"F0.imprint","INTERSECT",VERTEX,{"derivedFrom":[subQ1,subQ0]});Q16=makeQuery(id+"F0.imprint","IMPRINT",FACE,{"disambiguationData":[TD([[makeQuery(id+"F0.imprint","IMPRINT",EDGE,{"disambiguationData":[TD([[subQ2,-1.0]])],"derivedFrom":subQ1}),1.0]])]});}
            var Q17;
            {var subQ0=sQuery(id+"F0.wireOp",EDGE,"E31");var subQ1=sQuery(id+"F0.wireOp",EDGE,"E8");var subQ2=makeQuery(id+"F0.imprint","INTERSECT",VERTEX,{"derivedFrom":[subQ1,subQ0]});Q17=makeQuery(id+"F0.imprint","IMPRINT",FACE,{"disambiguationData":[TD([[makeQuery(id+"F0.imprint","IMPRINT",EDGE,{"disambiguationData":[TD([[subQ2,-1.0]])],"derivedFrom":subQ1}),1.0]])]});}
            var Q18;
            {var subQ0=sQuery(id+"F0.wireOp",EDGE,"E30");var subQ1=sQuery(id+"F0.wireOp",EDGE,"E8");var subQ2=makeQuery(id+"F0.imprint","INTERSECT",VERTEX,{"derivedFrom":[subQ1,subQ0]});Q18=makeQuery(id+"F0.imprint","IMPRINT",FACE,{"disambiguationData":[TD([[makeQuery(id+"F0.imprint","IMPRINT",EDGE,{"disambiguationData":[TD([[subQ2,-1.0]])],"derivedFrom":subQ1}),1.0]])]});}
            var Q19;
            {var subQ0=sQuery(id+"F0.wireOp",EDGE,"E30");var subQ1=sQuery(id+"F0.wireOp",EDGE,"E6");var subQ2=makeQuery(id+"F0.imprint","INTERSECT",VERTEX,{"derivedFrom":[subQ1,subQ0]});Q19=makeQuery(id+"F0.imprint","IMPRINT",FACE,{"disambiguationData":[TD([[makeQuery(id+"F0.imprint","IMPRINT",EDGE,{"disambiguationData":[TD([[subQ2,-1.0]])],"derivedFrom":subQ1}),1.0]])]});}
            var Q20;
            {var subQ0=sQuery(id+"F0.wireOp",EDGE,"E31");var subQ1=sQuery(id+"F0.wireOp",EDGE,"E6");var subQ2=makeQuery(id+"F0.imprint","INTERSECT",VERTEX,{"derivedFrom":[subQ1,subQ0]});Q20=makeQuery(id+"F0.imprint","IMPRINT",FACE,{"disambiguationData":[TD([[makeQuery(id+"F0.imprint","IMPRINT",EDGE,{"disambiguationData":[TD([[subQ2,-1.0]])],"derivedFrom":subQ1}),1.0]])]});}
            var Q21;
            {var subQ0=sQuery(id+"F0.wireOp",EDGE,"E32");var subQ1=sQuery(id+"F0.wireOp",EDGE,"E6");var subQ2=makeQuery(id+"F0.imprint","INTERSECT",VERTEX,{"derivedFrom":[subQ1,subQ0]});Q21=makeQuery(id+"F0.imprint","IMPRINT",FACE,{"disambiguationData":[TD([[makeQuery(id+"F0.imprint","IMPRINT",EDGE,{"disambiguationData":[TD([[subQ2,-1.0]])],"derivedFrom":subQ1}),1.0]])]});}
            var Q22;
            {var subQ0=sQuery(id+"F0.wireOp",EDGE,"E33");var subQ1=sQuery(id+"F0.wireOp",EDGE,"E6");var subQ2=makeQuery(id+"F0.imprint","INTERSECT",VERTEX,{"derivedFrom":[subQ1,subQ0]});Q22=makeQuery(id+"F0.imprint","IMPRINT",FACE,{"disambiguationData":[TD([[makeQuery(id+"F0.imprint","IMPRINT",EDGE,{"disambiguationData":[TD([[subQ2,-1.0]])],"derivedFrom":subQ1}),1.0]])]});}
            var Q23;
            {var subQ0=sQuery(id+"F0.wireOp",EDGE,"E34");var subQ1=sQuery(id+"F0.wireOp",EDGE,"E6");var subQ2=makeQuery(id+"F0.imprint","INTERSECT",VERTEX,{"derivedFrom":[subQ1,subQ0]});Q23=makeQuery(id+"F0.imprint","IMPRINT",FACE,{"disambiguationData":[TD([[makeQuery(id+"F0.imprint","IMPRINT",EDGE,{"disambiguationData":[TD([[subQ2,-1.0]])],"derivedFrom":subQ1}),1.0]])]});}
            var Q24;
            {var subQ0=sQuery(id+"F0.wireOp",EDGE,"E36");var subQ1=sQuery(id+"F0.wireOp",EDGE,"E6");var subQ2=makeQuery(id+"F0.imprint","INTERSECT",VERTEX,{"derivedFrom":[subQ1,subQ0]});Q24=makeQuery(id+"F0.imprint","IMPRINT",FACE,{"disambiguationData":[TD([[makeQuery(id+"F0.imprint","IMPRINT",EDGE,{"disambiguationData":[TD([[subQ2,-1.0]])],"derivedFrom":subQ1}),1.0]])]});}
            var Q25;
            {var subQ0=sQuery(id+"F0.wireOp",EDGE,"E37");var subQ1=sQuery(id+"F0.wireOp",EDGE,"E6");var subQ2=makeQuery(id+"F0.imprint","INTERSECT",VERTEX,{"derivedFrom":[subQ1,subQ0]});Q25=makeQuery(id+"F0.imprint","IMPRINT",FACE,{"disambiguationData":[TD([[makeQuery(id+"F0.imprint","IMPRINT",EDGE,{"disambiguationData":[TD([[subQ2,-1.0]])],"derivedFrom":subQ1}),1.0]])]});}
            var Q26;
            {var subQ0=sQuery(id+"F0.wireOp",EDGE,"E38");var subQ1=sQuery(id+"F0.wireOp",EDGE,"E6");var subQ2=makeQuery(id+"F0.imprint","INTERSECT",VERTEX,{"derivedFrom":[subQ1,subQ0]});Q26=makeQuery(id+"F0.imprint","IMPRINT",FACE,{"disambiguationData":[TD([[makeQuery(id+"F0.imprint","IMPRINT",EDGE,{"disambiguationData":[TD([[subQ2,-1.0]])],"derivedFrom":subQ1}),1.0]])]});}
            var Q27;
            {var subQ0=sQuery(id+"F0.wireOp",EDGE,"E38");var subQ1=sQuery(id+"F0.wireOp",EDGE,"E8");var subQ2=makeQuery(id+"F0.imprint","INTERSECT",VERTEX,{"derivedFrom":[subQ1,subQ0]});Q27=makeQuery(id+"F0.imprint","IMPRINT",FACE,{"disambiguationData":[TD([[makeQuery(id+"F0.imprint","IMPRINT",EDGE,{"disambiguationData":[TD([[subQ2,-1.0]])],"derivedFrom":subQ1}),1.0]])]});}
            var Q28;
            {var subQ0=sQuery(id+"F0.wireOp",EDGE,"E39");var subQ1=sQuery(id+"F0.wireOp",EDGE,"E8");var subQ2=makeQuery(id+"F0.imprint","INTERSECT",VERTEX,{"derivedFrom":[subQ1,subQ0]});Q28=makeQuery(id+"F0.imprint","IMPRINT",FACE,{"disambiguationData":[TD([[makeQuery(id+"F0.imprint","IMPRINT",EDGE,{"disambiguationData":[TD([[subQ2,-1.0]])],"derivedFrom":subQ1}),1.0]])]});}
            var Q29;
            {var subQ0=sQuery(id+"F0.wireOp",EDGE,"E35");var subQ1=sQuery(id+"F0.wireOp",EDGE,"E6");var subQ2=makeQuery(id+"F0.imprint","INTERSECT",VERTEX,{"derivedFrom":[subQ1,subQ0]});Q29=makeQuery(id+"F0.imprint","IMPRINT",FACE,{"disambiguationData":[TD([[makeQuery(id+"F0.imprint","IMPRINT",EDGE,{"disambiguationData":[TD([[subQ2,-1.0]])],"derivedFrom":subQ1}),1.0]])]});}
            var Q30;
            {var subQ0=sQuery(id+"F0.wireOp",EDGE,"E29");var subQ1=sQuery(id+"F0.wireOp",EDGE,"E6");var subQ2=makeQuery(id+"F0.imprint","INTERSECT",VERTEX,{"derivedFrom":[subQ1,subQ0]});Q30=makeQuery(id+"F0.imprint","IMPRINT",FACE,{"disambiguationData":[TD([[makeQuery(id+"F0.imprint","IMPRINT",EDGE,{"disambiguationData":[TD([[subQ2,-1.0]])],"derivedFrom":subQ1}),1.0]])]});}
            var Q31;
            {var subQ0=sQuery(id+"F0.wireOp",EDGE,"E27");var subQ1=sQuery(id+"F0.wireOp",EDGE,"E6");var subQ2=makeQuery(id+"F0.imprint","INTERSECT",VERTEX,{"derivedFrom":[subQ1,subQ0]});Q31=makeQuery(id+"F0.imprint","IMPRINT",FACE,{"disambiguationData":[TD([[makeQuery(id+"F0.imprint","IMPRINT",EDGE,{"disambiguationData":[TD([[subQ2,-1.0]])],"derivedFrom":subQ1}),1.0]])]});}
            var Q32;
            {var subQ0=sQuery(id+"F0.wireOp",EDGE,"E26");var subQ1=sQuery(id+"F0.wireOp",EDGE,"E6");var subQ2=makeQuery(id+"F0.imprint","INTERSECT",VERTEX,{"derivedFrom":[subQ1,subQ0]});Q32=makeQuery(id+"F0.imprint","IMPRINT",FACE,{"disambiguationData":[TD([[makeQuery(id+"F0.imprint","IMPRINT",EDGE,{"disambiguationData":[TD([[subQ2,-1.0]])],"derivedFrom":subQ1}),1.0]])]});}
            var Q33;
            {var subQ0=sQuery(id+"F0.wireOp",EDGE,"E25");var subQ1=sQuery(id+"F0.wireOp",EDGE,"E6");var subQ2=makeQuery(id+"F0.imprint","INTERSECT",VERTEX,{"derivedFrom":[subQ1,subQ0]});Q33=makeQuery(id+"F0.imprint","IMPRINT",FACE,{"disambiguationData":[TD([[makeQuery(id+"F0.imprint","IMPRINT",EDGE,{"disambiguationData":[TD([[subQ2,-1.0]])],"derivedFrom":subQ1}),1.0]])]});}
            var Q34;
            {var subQ0=sQuery(id+"F0.wireOp",EDGE,"E28");var subQ1=sQuery(id+"F0.wireOp",EDGE,"E6");var subQ2=makeQuery(id+"F0.imprint","INTERSECT",VERTEX,{"derivedFrom":[subQ1,subQ0]});Q34=makeQuery(id+"F0.imprint","IMPRINT",FACE,{"disambiguationData":[TD([[makeQuery(id+"F0.imprint","IMPRINT",EDGE,{"disambiguationData":[TD([[subQ2,-1.0]])],"derivedFrom":subQ1}),1.0]])]});}
            var Q35;
            {var subQ0=sQuery(id+"F0.wireOp",EDGE,"E24");var subQ1=sQuery(id+"F0.wireOp",EDGE,"E6");var subQ2=makeQuery(id+"F0.imprint","INTERSECT",VERTEX,{"derivedFrom":[subQ1,subQ0]});Q35=makeQuery(id+"F0.imprint","IMPRINT",FACE,{"disambiguationData":[TD([[makeQuery(id+"F0.imprint","IMPRINT",EDGE,{"disambiguationData":[TD([[subQ2,-1.0]])],"derivedFrom":subQ1}),1.0]])]});}
            var Q36;
            {var subQ0=sQuery(id+"F0.wireOp",EDGE,"E24");var subQ1=sQuery(id+"F0.wireOp",EDGE,"E8");var subQ2=makeQuery(id+"F0.imprint","INTERSECT",VERTEX,{"derivedFrom":[subQ1,subQ0]});Q36=makeQuery(id+"F0.imprint","IMPRINT",FACE,{"disambiguationData":[TD([[makeQuery(id+"F0.imprint","IMPRINT",EDGE,{"disambiguationData":[TD([[subQ2,-1.0]])],"derivedFrom":subQ1}),1.0]])]});}
            var Q37;
            {var subQ0=sQuery(id+"F0.wireOp",EDGE,"E28");var subQ1=sQuery(id+"F0.wireOp",EDGE,"E8");var subQ2=makeQuery(id+"F0.imprint","INTERSECT",VERTEX,{"derivedFrom":[subQ1,subQ0]});Q37=makeQuery(id+"F0.imprint","IMPRINT",FACE,{"disambiguationData":[TD([[makeQuery(id+"F0.imprint","IMPRINT",EDGE,{"disambiguationData":[TD([[subQ2,-1.0]])],"derivedFrom":subQ1}),1.0]])]});}
            var Q38;
            {var subQ0=sQuery(id+"F0.wireOp",EDGE,"E25");var subQ1=sQuery(id+"F0.wireOp",EDGE,"E8");var subQ2=makeQuery(id+"F0.imprint","INTERSECT",VERTEX,{"derivedFrom":[subQ1,subQ0]});Q38=makeQuery(id+"F0.imprint","IMPRINT",FACE,{"disambiguationData":[TD([[makeQuery(id+"F0.imprint","IMPRINT",EDGE,{"disambiguationData":[TD([[subQ2,-1.0]])],"derivedFrom":subQ1}),1.0]])]});}
            var Q39;
            {var subQ0=sQuery(id+"F0.wireOp",EDGE,"E26");var subQ1=sQuery(id+"F0.wireOp",EDGE,"E8");var subQ2=makeQuery(id+"F0.imprint","INTERSECT",VERTEX,{"derivedFrom":[subQ1,subQ0]});Q39=makeQuery(id+"F0.imprint","IMPRINT",FACE,{"disambiguationData":[TD([[makeQuery(id+"F0.imprint","IMPRINT",EDGE,{"disambiguationData":[TD([[subQ2,-1.0]])],"derivedFrom":subQ1}),1.0]])]});}
            var Q40;
            {var subQ0=sQuery(id+"F0.wireOp",EDGE,"E27");var subQ1=sQuery(id+"F0.wireOp",EDGE,"E8");var subQ2=makeQuery(id+"F0.imprint","INTERSECT",VERTEX,{"derivedFrom":[subQ1,subQ0]});Q40=makeQuery(id+"F0.imprint","IMPRINT",FACE,{"disambiguationData":[TD([[makeQuery(id+"F0.imprint","IMPRINT",EDGE,{"disambiguationData":[TD([[subQ2,-1.0]])],"derivedFrom":subQ1}),1.0]])]});}
            var Q41;
            {var subQ0=sQuery(id+"F0.wireOp",EDGE,"E29");var subQ1=sQuery(id+"F0.wireOp",EDGE,"E8");var subQ2=makeQuery(id+"F0.imprint","INTERSECT",VERTEX,{"derivedFrom":[subQ1,subQ0]});Q41=makeQuery(id+"F0.imprint","IMPRINT",FACE,{"disambiguationData":[TD([[makeQuery(id+"F0.imprint","IMPRINT",EDGE,{"disambiguationData":[TD([[subQ2,-1.0]])],"derivedFrom":subQ1}),1.0]])]});}
            var Q42;
            {var subQ0=sQuery(id+"F0.wireOp",EDGE,"E13");var subQ1=sQuery(id+"F0.wireOp",EDGE,"E6");var subQ2=makeQuery(id+"F0.imprint","INTERSECT",VERTEX,{"derivedFrom":[subQ1,subQ0]});Q42=makeQuery(id+"F0.imprint","IMPRINT",FACE,{"disambiguationData":[TD([[makeQuery(id+"F0.imprint","IMPRINT",EDGE,{"disambiguationData":[TD([[subQ2,-1.0]])],"derivedFrom":subQ1}),1.0]])]});}
            var Q43;
            {var subQ0=sQuery(id+"F0.wireOp",EDGE,"E14");var subQ1=sQuery(id+"F0.wireOp",EDGE,"E6");var subQ2=makeQuery(id+"F0.imprint","INTERSECT",VERTEX,{"derivedFrom":[subQ1,subQ0]});Q43=makeQuery(id+"F0.imprint","IMPRINT",FACE,{"disambiguationData":[TD([[makeQuery(id+"F0.imprint","IMPRINT",EDGE,{"disambiguationData":[TD([[subQ2,-1.0]])],"derivedFrom":subQ1}),1.0]])]});}
            var Q44;
            {var subQ0=sQuery(id+"F0.wireOp",EDGE,"E15");var subQ1=sQuery(id+"F0.wireOp",EDGE,"E6");var subQ2=makeQuery(id+"F0.imprint","INTERSECT",VERTEX,{"derivedFrom":[subQ1,subQ0]});Q44=makeQuery(id+"F0.imprint","IMPRINT",FACE,{"disambiguationData":[TD([[makeQuery(id+"F0.imprint","IMPRINT",EDGE,{"disambiguationData":[TD([[subQ2,-1.0]])],"derivedFrom":subQ1}),1.0]])]});}
            var Q45;
            {var subQ0=sQuery(id+"F0.wireOp",EDGE,"E16");var subQ1=sQuery(id+"F0.wireOp",EDGE,"E6");var subQ2=makeQuery(id+"F0.imprint","INTERSECT",VERTEX,{"derivedFrom":[subQ1,subQ0]});Q45=makeQuery(id+"F0.imprint","IMPRINT",FACE,{"disambiguationData":[TD([[makeQuery(id+"F0.imprint","IMPRINT",EDGE,{"disambiguationData":[TD([[subQ2,-1.0]])],"derivedFrom":subQ1}),1.0]])]});}
            var Q46;
            {var subQ0=sQuery(id+"F0.wireOp",EDGE,"E17");var subQ1=sQuery(id+"F0.wireOp",EDGE,"E6");var subQ2=makeQuery(id+"F0.imprint","INTERSECT",VERTEX,{"derivedFrom":[subQ1,subQ0]});Q46=makeQuery(id+"F0.imprint","IMPRINT",FACE,{"disambiguationData":[TD([[makeQuery(id+"F0.imprint","IMPRINT",EDGE,{"disambiguationData":[TD([[subQ2,-1.0]])],"derivedFrom":subQ1}),1.0]])]});}
            var Q47;
            {var subQ0=sQuery(id+"F0.wireOp",EDGE,"E18");var subQ1=sQuery(id+"F0.wireOp",EDGE,"E6");var subQ2=makeQuery(id+"F0.imprint","INTERSECT",VERTEX,{"derivedFrom":[subQ1,subQ0]});Q47=makeQuery(id+"F0.imprint","IMPRINT",FACE,{"disambiguationData":[TD([[makeQuery(id+"F0.imprint","IMPRINT",EDGE,{"disambiguationData":[TD([[subQ2,-1.0]])],"derivedFrom":subQ1}),1.0]])]});}
            var Q48;
            {var subQ0=sQuery(id+"F0.wireOp",EDGE,"E19");var subQ1=sQuery(id+"F0.wireOp",EDGE,"E6");var subQ2=makeQuery(id+"F0.imprint","INTERSECT",VERTEX,{"derivedFrom":[subQ1,subQ0]});Q48=makeQuery(id+"F0.imprint","IMPRINT",FACE,{"disambiguationData":[TD([[makeQuery(id+"F0.imprint","IMPRINT",EDGE,{"disambiguationData":[TD([[subQ2,-1.0]])],"derivedFrom":subQ1}),1.0]])]});}
            var Q49;
            {var subQ0=sQuery(id+"F0.wireOp",EDGE,"E22");var subQ1=sQuery(id+"F0.wireOp",EDGE,"E6");var subQ2=makeQuery(id+"F0.imprint","INTERSECT",VERTEX,{"derivedFrom":[subQ1,subQ0]});Q49=makeQuery(id+"F0.imprint","IMPRINT",FACE,{"disambiguationData":[TD([[makeQuery(id+"F0.imprint","IMPRINT",EDGE,{"disambiguationData":[TD([[subQ2,-1.0]])],"derivedFrom":subQ1}),1.0]])]});}
            var Q50;
            {var subQ0=sQuery(id+"F0.wireOp",EDGE,"E23");var subQ1=sQuery(id+"F0.wireOp",EDGE,"E6");var subQ2=makeQuery(id+"F0.imprint","INTERSECT",VERTEX,{"derivedFrom":[subQ1,subQ0]});Q50=makeQuery(id+"F0.imprint","IMPRINT",FACE,{"disambiguationData":[TD([[makeQuery(id+"F0.imprint","IMPRINT",EDGE,{"disambiguationData":[TD([[subQ2,-1.0]])],"derivedFrom":subQ1}),1.0]])]});}
            var Q51;
            {var subQ0=sQuery(id+"F0.wireOp",EDGE,"E23");var subQ1=sQuery(id+"F0.wireOp",EDGE,"E8");var subQ2=makeQuery(id+"F0.imprint","INTERSECT",VERTEX,{"derivedFrom":[subQ1,subQ0]});Q51=makeQuery(id+"F0.imprint","IMPRINT",FACE,{"disambiguationData":[TD([[makeQuery(id+"F0.imprint","IMPRINT",EDGE,{"disambiguationData":[TD([[subQ2,-1.0]])],"derivedFrom":subQ1}),1.0]])]});}
            var Q52;
            {var subQ0=sQuery(id+"F0.wireOp",EDGE,"E20");var subQ1=sQuery(id+"F0.wireOp",EDGE,"E8");var subQ2=makeQuery(id+"F0.imprint","INTERSECT",VERTEX,{"derivedFrom":[subQ1,subQ0]});Q52=makeQuery(id+"F0.imprint","IMPRINT",FACE,{"disambiguationData":[TD([[makeQuery(id+"F0.imprint","IMPRINT",EDGE,{"disambiguationData":[TD([[subQ2,-1.0]])],"derivedFrom":subQ1}),1.0]])]});}
            var Q53;
            {var subQ0=sQuery(id+"F0.wireOp",EDGE,"E17");var subQ1=sQuery(id+"F0.wireOp",EDGE,"E8");var subQ2=makeQuery(id+"F0.imprint","INTERSECT",VERTEX,{"derivedFrom":[subQ1,subQ0]});Q53=makeQuery(id+"F0.imprint","IMPRINT",FACE,{"disambiguationData":[TD([[makeQuery(id+"F0.imprint","IMPRINT",EDGE,{"disambiguationData":[TD([[subQ2,-1.0]])],"derivedFrom":subQ1}),1.0]])]});}
            var Q54;
            {var subQ0=sQuery(id+"F0.wireOp",EDGE,"E16");var subQ1=sQuery(id+"F0.wireOp",EDGE,"E8");var subQ2=makeQuery(id+"F0.imprint","INTERSECT",VERTEX,{"derivedFrom":[subQ1,subQ0]});Q54=makeQuery(id+"F0.imprint","IMPRINT",FACE,{"disambiguationData":[TD([[makeQuery(id+"F0.imprint","IMPRINT",EDGE,{"disambiguationData":[TD([[subQ2,-1.0]])],"derivedFrom":subQ1}),1.0]])]});}
            var Q55;
            {var subQ0=sQuery(id+"F0.wireOp",EDGE,"E15");var subQ1=sQuery(id+"F0.wireOp",EDGE,"E8");var subQ2=makeQuery(id+"F0.imprint","INTERSECT",VERTEX,{"derivedFrom":[subQ1,subQ0]});Q55=makeQuery(id+"F0.imprint","IMPRINT",FACE,{"disambiguationData":[TD([[makeQuery(id+"F0.imprint","IMPRINT",EDGE,{"disambiguationData":[TD([[subQ2,-1.0]])],"derivedFrom":subQ1}),1.0]])]});}
            var Q56;
            {var subQ0=sQuery(id+"F0.wireOp",EDGE,"E14");var subQ1=sQuery(id+"F0.wireOp",EDGE,"E8");var subQ2=makeQuery(id+"F0.imprint","INTERSECT",VERTEX,{"derivedFrom":[subQ1,subQ0]});Q56=makeQuery(id+"F0.imprint","IMPRINT",FACE,{"disambiguationData":[TD([[makeQuery(id+"F0.imprint","IMPRINT",EDGE,{"disambiguationData":[TD([[subQ2,-1.0]])],"derivedFrom":subQ1}),1.0]])]});}
            var Q57;
            {var subQ0=sQuery(id+"F0.wireOp",EDGE,"E13");var subQ1=sQuery(id+"F0.wireOp",EDGE,"E8");var subQ2=makeQuery(id+"F0.imprint","INTERSECT",VERTEX,{"derivedFrom":[subQ1,subQ0]});Q57=makeQuery(id+"F0.imprint","IMPRINT",FACE,{"disambiguationData":[TD([[makeQuery(id+"F0.imprint","IMPRINT",EDGE,{"disambiguationData":[TD([[subQ2,-1.0]])],"derivedFrom":subQ1}),1.0]])]});}
            var Q58;
            {var subQ0=sQuery(id+"F0.wireOp",EDGE,"E18");var subQ1=sQuery(id+"F0.wireOp",EDGE,"E8");var subQ2=makeQuery(id+"F0.imprint","INTERSECT",VERTEX,{"derivedFrom":[subQ1,subQ0]});Q58=makeQuery(id+"F0.imprint","IMPRINT",FACE,{"disambiguationData":[TD([[makeQuery(id+"F0.imprint","IMPRINT",EDGE,{"disambiguationData":[TD([[subQ2,-1.0]])],"derivedFrom":subQ1}),1.0]])]});}
            var Q59;
            {var subQ0=sQuery(id+"F0.wireOp",EDGE,"E19");var subQ7=sQuery(id+"F0.wireOp",EDGE,"E8");var subQ11=makeQuery(id+"F0.imprint","INTERSECT",VERTEX,{"derivedFrom":[subQ7,subQ0]});Q59=makeQuery(id+"F0.imprint","IMPRINT",FACE,{"disambiguationData":[TD([[makeQuery(id+"F0.imprint","IMPRINT",EDGE,{"disambiguationData":[TD([[subQ11,-1.0]])],"derivedFrom":subQ7}),1.0]])]});}
            var Q60;
            {var subQ0=sQuery(id+"F0.wireOp",EDGE,"E21");var subQ1=sQuery(id+"F0.wireOp",EDGE,"E8");var subQ2=makeQuery(id+"F0.imprint","INTERSECT",VERTEX,{"derivedFrom":[subQ1,subQ0]});Q60=makeQuery(id+"F0.imprint","IMPRINT",FACE,{"disambiguationData":[TD([[makeQuery(id+"F0.imprint","IMPRINT",EDGE,{"disambiguationData":[TD([[subQ2,-1.0]])],"derivedFrom":subQ1}),1.0]])]});}
            var Q61;
            {var subQ0=sQuery(id+"F0.wireOp",EDGE,"E22");var subQ1=sQuery(id+"F0.wireOp",EDGE,"E8");var subQ2=makeQuery(id+"F0.imprint","INTERSECT",VERTEX,{"derivedFrom":[subQ1,subQ0]});Q61=makeQuery(id+"F0.imprint","IMPRINT",FACE,{"disambiguationData":[TD([[makeQuery(id+"F0.imprint","IMPRINT",EDGE,{"disambiguationData":[TD([[subQ2,-1.0]])],"derivedFrom":subQ1}),1.0]])]});}
            var Q62;
            {var subQ0=sQuery(id+"F0.wireOp",EDGE,"E20");var subQ1=sQuery(id+"F0.wireOp",EDGE,"E6");var subQ2=makeQuery(id+"F0.imprint","INTERSECT",VERTEX,{"derivedFrom":[subQ1,subQ0]});Q62=makeQuery(id+"F0.imprint","IMPRINT",FACE,{"disambiguationData":[TD([[makeQuery(id+"F0.imprint","IMPRINT",EDGE,{"disambiguationData":[TD([[subQ2,-1.0]])],"derivedFrom":subQ1}),1.0]])]});}
            var Q63;
            {var subQ0=sQuery(id+"F0.wireOp",EDGE,"E21");var subQ1=sQuery(id+"F0.wireOp",EDGE,"E6");var subQ2=makeQuery(id+"F0.imprint","INTERSECT",VERTEX,{"derivedFrom":[subQ1,subQ0]});Q63=makeQuery(id+"F0.imprint","IMPRINT",FACE,{"disambiguationData":[TD([[makeQuery(id+"F0.imprint","IMPRINT",EDGE,{"disambiguationData":[TD([[subQ2,-1.0]])],"derivedFrom":subQ1}),1.0]])]});}
            extrude(context, id + "F6", {"entities" : qUnion([Q0, Q1, Q2, Q3, Q4, Q5, Q6, Q7, Q8, Q9, Q10, Q11, Q12, Q13, Q14, Q15, Q16, Q17, Q18, Q19, Q20, Q21, Q22, Q23, Q24, Q25, Q26, Q27, Q28, Q29, Q30, Q31, Q32, Q33, Q34, Q35, Q36, Q37, Q38, Q39, Q40, Q41, Q42, Q43, Q44, Q45, Q46, Q47, Q48, Q49, Q50, Q51, Q52, Q53, Q54, Q55, Q56, Q57, Q58, Q59, Q60, Q61, Q62, Q63]), "depth" : 2 * mm, "offsetDistance" : 25 * mm});
        }
        {
            var Q0;
            {var subQ0=sQuery(id+"F0.wireOp",EDGE,"E0.bottom");Q0=makeQuery(id+"F6.opExtrude","CAP_EDGE",EDGE,{"disambiguationData":[OSD([subQ0]),TDD([makeQuery(id+"F0.imprint","IMPRINT",EDGE,{"disambiguationData":[TD([[makeQuery(id+"F0.imprint","INTERSECT",VERTEX,{"derivedFrom":[subQ0,sQuery(id+"F0.wireOp",EDGE,"E8")]}),-1.0]])],"derivedFrom":subQ0})])],"isStart":false});}
            var Q1;
            {var subQ0=sQuery(id+"F0.wireOp",EDGE,"E0.bottom");Q1=makeQuery(id+"F6.opExtrude","CAP_EDGE",EDGE,{"disambiguationData":[OSD([subQ0]),TDD([makeQuery(id+"F0.imprint","IMPRINT",EDGE,{"disambiguationData":[TD([[makeQuery(id+"F0.imprint","INTERSECT",VERTEX,{"derivedFrom":[subQ0,sQuery(id+"F0.wireOp",EDGE,"E6")]}),-1.0]])],"derivedFrom":subQ0})])],"isStart":false});}
            chamfer(context, id + "F7", {"entities" : qUnion([Q0, Q1]), "chamferType" : ChamferType.TWO_OFFSETS, "width1" : 1 * mm, "oppositeDirection" : false, "width2" : 2.5 * mm, "tangentPropagation" : true});
        }
        {
            var Q0;
            {var subQ0=sQuery(id+"F0.wireOp",EDGE,"E0.bottom");Q0=makeQuery(id+"F1.opExtrude","CAP_EDGE",EDGE,{"disambiguationData":[OSD([subQ0]),TDD([makeQuery(id+"F0.imprint","IMPRINT",EDGE,{"disambiguationData":[TD([[makeQuery(id+"F0.imprint","INTERSECT",VERTEX,{"derivedFrom":[subQ0,sQuery(id+"F0.wireOp",EDGE,"E7")]}),-1.0]])],"derivedFrom":subQ0})])],"isStart":false});}
            chamfer(context, id + "F8", {"entities" : qUnion([Q0]), "chamferType" : ChamferType.TWO_OFFSETS, "width1" : 2 * mm, "oppositeDirection" : false, "width2" : 5 * mm, "tangentPropagation" : true});
        }
        {
            var Q0;
            {var subQ0=sQuery(id+"F0.wireOp",EDGE,"E0.top");Q0=makeQuery(id+"F6.opExtrude","CAP_EDGE",EDGE,{"disambiguationData":[OSD([subQ0]),TDD([makeQuery(id+"F0.imprint","IMPRINT",EDGE,{"disambiguationData":[TD([[makeQuery(id+"F0.imprint","INTERSECT",VERTEX,{"derivedFrom":[subQ0,sQuery(id+"F0.wireOp",EDGE,"E6")]}),-1.0]])],"derivedFrom":subQ0})])],"isStart":false});}
            var Q1;
            {var subQ0=sQuery(id+"F0.wireOp",EDGE,"E0.top");Q1=makeQuery(id+"F6.opExtrude","CAP_EDGE",EDGE,{"disambiguationData":[OSD([subQ0]),TDD([makeQuery(id+"F0.imprint","IMPRINT",EDGE,{"disambiguationData":[TD([[makeQuery(id+"F0.imprint","INTERSECT",VERTEX,{"derivedFrom":[subQ0,sQuery(id+"F0.wireOp",EDGE,"E8")]}),-1.0]])],"derivedFrom":subQ0})])],"isStart":false});}
            chamfer(context, id + "F9", {"entities" : qUnion([Q0, Q1]), "chamferType" : ChamferType.TWO_OFFSETS, "width1" : 2.5 * mm, "oppositeDirection" : false, "width2" : 1 * mm, "tangentPropagation" : true});
        }
    });
